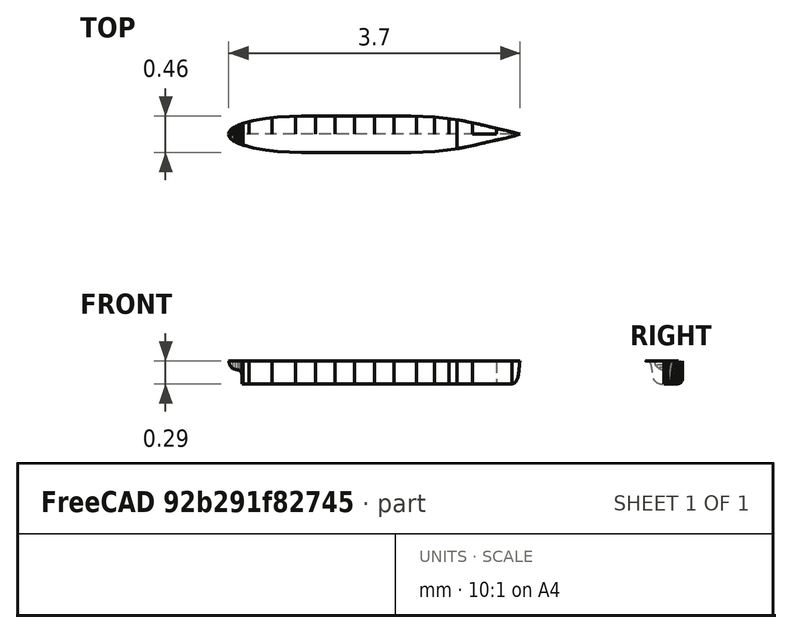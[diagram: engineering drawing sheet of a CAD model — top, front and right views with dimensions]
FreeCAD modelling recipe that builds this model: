
FCSTD DOCUMENT  (FreeCAD 0.21R33771 (Git))
Label: vessel_c
License: All rights reserved
LicenseURL: http://en.wikipedia.org/wiki/All_rights_reserved
objects: Sketcher::SketchObject×36, Part::FeaturePython×20, Surface::Sections×4, Part::Mirroring×2, PartDesign::Body×1, Surface::GeomFillSurface×1, Part::Compound×1
note: 65 computed .brp shape members not serialized (recipe doc carries the construction recipe); baked Part::Feature solids carry a one-line shape summary decoded from their .brp

FEATURE [Sketcher::SketchObject] Sketch
  AttachmentOffset = pos=(0,0,1.849) rot=(0,0,1;0rad)
  FullyConstrained = true
  MapMode = 5
  Placement = pos=(1.849,-4e-16,4e-16) rot=(0.57735,0.57735,0.57735;2.0944rad)
  Support = -> [YZ_Plane]
  sketch-geometry (11):
    g0: LineSegment StartX=0 StartY=0 StartZ=0 EndX=0.1677 EndY=0 EndZ=0
    g1: LineSegment StartX=0 StartY=0.03 StartZ=0 EndX=0.22441 EndY=0.03 EndZ=0
    g2: LineSegment StartX=0 StartY=0.06 StartZ=0 EndX=0.23332 EndY=0.06 EndZ=0
    g3: LineSegment StartX=0 StartY=0.09 StartZ=0 EndX=0.23332 EndY=0.09 EndZ=0
    g4: LineSegment StartX=0 StartY=0.15 StartZ=0 EndX=0.23332 EndY=0.15 EndZ=0
    g5: LineSegment StartX=0 StartY=0.12 StartZ=0 EndX=0.23332 EndY=0.12 EndZ=0
    g6: LineSegment StartX=0 StartY=0.18 StartZ=0 EndX=0.23332 EndY=0.18 EndZ=0
    g7: LineSegment StartX=0 StartY=0.21 StartZ=0 EndX=0.23332 EndY=0.21 EndZ=0
    g8: LineSegment StartX=0 StartY=0.24 StartZ=0 EndX=0.23332 EndY=0.24 EndZ=0
    g9: LineSegment StartX=0 StartY=0.28956 StartZ=0 EndX=0.23332 EndY=0.28956 EndZ=0
    g10: LineSegment StartX=0 StartY=0.27 StartZ=0 EndX=0.23332 EndY=0.27 EndZ=0
  constraints (43):
    c: Coincident(g0,g-1)
    c: PointOnObject(g0,g-1)
    c: PointOnObject(g1,g-2)
    c: Horizontal(g1)
    c: PointOnObject(g2,g-2)
    c: Horizontal(g2)
    c: PointOnObject(g3,g-2)
    c: Horizontal(g3)
    c: PointOnObject(g4,g-2)
    c: Horizontal(g4)
    c: PointOnObject(g5,g-2)
    c: Horizontal(g5)
    c: PointOnObject(g6,g-2)
    c: Horizontal(g6)
    c: PointOnObject(g7,g-2)
    c: Horizontal(g7)
    c: PointOnObject(g8,g-2)
    c: Horizontal(g8)
    c: PointOnObject(g9,g-2)
    c: Horizontal(g9)
    c: DistanceY(g0,g1) = 0.03
    c: DistanceY(g0,g2) = 0.06
    c: DistanceY(g0,g3) = 0.09
    c: DistanceY(g0,g5) = 0.12
    c: DistanceY(g0,g4) = 0.15
    c: DistanceY(g0,g6) = 0.18
    c: DistanceY(g0,g7) = 0.21
    c: DistanceY(g0,g8) = 0.24
    c: DistanceY(g0,g9) = 0.28956
    c: DistanceX(g9,g9) = 0.23332
    c: DistanceX(g8,g8) = 0.23332
    c: DistanceX(g7,g7) = 0.23332
    c: DistanceX(g6,g6) = 0.23332
    c: DistanceX(g4,g4) = 0.23332
    c: DistanceX(g5,g5) = 0.23332
    c: DistanceX(g3,g3) = 0.23332
    c: DistanceX(g2,g2) = 0.23332
    c: DistanceX(g1,g1) = 0.22441
    c: DistanceX(g0,g0) = 0.1677
    c: PointOnObject(g10,g-2)
    c: Horizontal(g10)
    c: DistanceY(g0,g10) = 0.27
    c: DistanceX(g10,g10) = 0.23332
FEATURE [Sketcher::SketchObject] Sketch001
  AttachmentOffset = pos=(0,0,1.59904) rot=(0,0,1;0rad)
  FullyConstrained = true
  MapMode = 5
  Placement = pos=(1.59904,-4e-16,4e-16) rot=(0.57735,0.57735,0.57735;2.0944rad)
  Support = -> [YZ_Plane]
  expr: Constraints[20] = Sketch.Constraints[20]
  expr: Constraints[21] = Sketch.Constraints[21]
  expr: Constraints[22] = Sketch.Constraints[22]
  expr: Constraints[23] = Sketch.Constraints[23]
  expr: Constraints[24] = Sketch.Constraints[24]
  expr: Constraints[25] = Sketch.Constraints[25]
  expr: Constraints[26] = Sketch.Constraints[26]
  expr: Constraints[27] = Sketch.Constraints[27]
  expr: Constraints[28] = Sketch.Constraints[28]
  expr: Constraints[31] = Sketch.Constraints[41]
  sketch-geometry (11):
    g0: LineSegment StartX=0 StartY=0 StartZ=0 EndX=0.15932 EndY=0 EndZ=0
    g1: LineSegment StartX=0 StartY=0.03 StartZ=0 EndX=0.22247 EndY=0.03 EndZ=0
    g2: LineSegment StartX=0 StartY=0.06 StartZ=0 EndX=0.23305 EndY=0.06 EndZ=0
    g3: LineSegment StartX=0 StartY=0.09 StartZ=0 EndX=0.23375 EndY=0.09 EndZ=0
    g4: LineSegment StartX=0 StartY=0.15 StartZ=0 EndX=0.2335 EndY=0.15 EndZ=0
    g5: LineSegment StartX=0 StartY=0.12 StartZ=0 EndX=0.23366 EndY=0.12 EndZ=0
    g6: LineSegment StartX=0 StartY=0.18 StartZ=0 EndX=0.23339 EndY=0.18 EndZ=0
    g7: LineSegment StartX=0 StartY=0.21 StartZ=0 EndX=0.23332 EndY=0.21 EndZ=0
    g8: LineSegment StartX=0 StartY=0.24 StartZ=0 EndX=0.23329 EndY=0.24 EndZ=0
    g9: LineSegment StartX=0 StartY=0.28956 StartZ=0 EndX=0.23334 EndY=0.28956 EndZ=0
    g10: LineSegment StartX=0 StartY=0.27 StartZ=0 EndX=0.23332 EndY=0.27 EndZ=0
  constraints (43):
    c: Coincident(g0,g-1)
    c: PointOnObject(g0,g-1)
    c: PointOnObject(g1,g-2)
    c: Horizontal(g1)
    c: PointOnObject(g2,g-2)
    c: Horizontal(g2)
    c: PointOnObject(g3,g-2)
    c: Horizontal(g3)
    c: PointOnObject(g4,g-2)
    c: Horizontal(g4)
    c: PointOnObject(g5,g-2)
    c: Horizontal(g5)
    c: PointOnObject(g6,g-2)
    c: Horizontal(g6)
    c: PointOnObject(g7,g-2)
    c: Horizontal(g7)
    c: PointOnObject(g8,g-2)
    c: Horizontal(g8)
    c: PointOnObject(g9,g-2)
    c: Horizontal(g9)
    c: DistanceY(g0,g1) = 0.03
    c: DistanceY(g0,g2) = 0.06
    c: DistanceY(g0,g3) = 0.09
    c: DistanceY(g0,g5) = 0.12
    c: DistanceY(g0,g4) = 0.15
    c: DistanceY(g0,g6) = 0.18
    c: DistanceY(g0,g7) = 0.21
    c: DistanceY(g0,g8) = 0.24
    c: DistanceY(g0,g9) = 0.28956
    c: PointOnObject(g10,g-2)
    c: Horizontal(g10)
    c: DistanceY(g0,g10) = 0.27
    c: DistanceX(g9,g9) = 0.23334
    c: DistanceX(g10,g10) = 0.23332
    c: DistanceX(g8,g8) = 0.23329
    c: DistanceX(g7,g7) = 0.23332
    c: DistanceX(g6,g6) = 0.23339
    c: DistanceX(g4,g4) = 0.2335
    c: DistanceX(g5,g5) = 0.23366
    c: DistanceX(g3,g3) = 0.23375
    c: DistanceX(g2,g2) = 0.23305
    c: DistanceX(g1,g1) = 0.22247
    c: DistanceX(g0,g0) = 0.15932
FEATURE [Sketcher::SketchObject] Sketch002
  AttachmentOffset = pos=(0,0,1.34904) rot=(0,0,1;0rad)
  FullyConstrained = true
  MapMode = 5
  Placement = pos=(1.34904,-3e-16,3e-16) rot=(0.57735,0.57735,0.57735;2.0944rad)
  Support = -> [YZ_Plane]
  expr: Constraints[20] = Sketch.Constraints[20]
  expr: Constraints[21] = Sketch.Constraints[21]
  expr: Constraints[22] = Sketch.Constraints[22]
  expr: Constraints[23] = Sketch.Constraints[23]
  expr: Constraints[24] = Sketch.Constraints[24]
  expr: Constraints[25] = Sketch.Constraints[25]
  expr: Constraints[26] = Sketch.Constraints[26]
  expr: Constraints[27] = Sketch.Constraints[27]
  expr: Constraints[28] = Sketch.Constraints[28]
  expr: Constraints[31] = Sketch.Constraints[41]
  sketch-geometry (11):
    g0: LineSegment StartX=0 StartY=0 StartZ=0 EndX=0.14688 EndY=0 EndZ=0
    g1: LineSegment StartX=0 StartY=0.03 StartZ=0 EndX=0.20812 EndY=0.03 EndZ=0
    g2: LineSegment StartX=0 StartY=0.06 StartZ=0 EndX=0.2252 EndY=0.06 EndZ=0
    g3: LineSegment StartX=0 StartY=0.09 StartZ=0 EndX=0.23076 EndY=0.09 EndZ=0
    g4: LineSegment StartX=0 StartY=0.15 StartZ=0 EndX=0.23278 EndY=0.15 EndZ=0
    g5: LineSegment StartX=0 StartY=0.12 StartZ=0 EndX=0.23256 EndY=0.12 EndZ=0
    g6: LineSegment StartX=0 StartY=0.18 StartZ=0 EndX=0.23278 EndY=0.18 EndZ=0
    g7: LineSegment StartX=0 StartY=0.21 StartZ=0 EndX=0.23286 EndY=0.21 EndZ=0
    g8: LineSegment StartX=0 StartY=0.24 StartZ=0 EndX=0.23303 EndY=0.24 EndZ=0
    g9: LineSegment StartX=0 StartY=0.28956 StartZ=0 EndX=0.23331 EndY=0.28956 EndZ=0
    g10: LineSegment StartX=0 StartY=0.27 StartZ=0 EndX=0.2332 EndY=0.27 EndZ=0
  constraints (43):
    c: Coincident(g0,g-1)
    c: PointOnObject(g0,g-1)
    c: PointOnObject(g1,g-2)
    c: Horizontal(g1)
    c: PointOnObject(g2,g-2)
    c: Horizontal(g2)
    c: PointOnObject(g3,g-2)
    c: Horizontal(g3)
    c: PointOnObject(g4,g-2)
    c: Horizontal(g4)
    c: PointOnObject(g5,g-2)
    c: Horizontal(g5)
    c: PointOnObject(g6,g-2)
    c: Horizontal(g6)
    c: PointOnObject(g7,g-2)
    c: Horizontal(g7)
    c: PointOnObject(g8,g-2)
    c: Horizontal(g8)
    c: PointOnObject(g9,g-2)
    c: Horizontal(g9)
    c: DistanceY(g0,g1) = 0.03
    c: DistanceY(g0,g2) = 0.06
    c: DistanceY(g0,g3) = 0.09
    c: DistanceY(g0,g5) = 0.12
    c: DistanceY(g0,g4) = 0.15
    c: DistanceY(g0,g6) = 0.18
    c: DistanceY(g0,g7) = 0.21
    c: DistanceY(g0,g8) = 0.24
    c: DistanceY(g0,g9) = 0.28956
    c: PointOnObject(g10,g-2)
    c: Horizontal(g10)
    c: DistanceY(g0,g10) = 0.27
    c: DistanceX(g9,g9) = 0.23331
    c: DistanceX(g10,g10) = 0.2332
    c: DistanceX(g8,g8) = 0.23303
    c: DistanceX(g7,g7) = 0.23286
    c: DistanceX(g6,g6) = 0.23278
    c: DistanceX(g4,g4) = 0.23278
    c: DistanceX(g5,g5) = 0.23256
    c: DistanceX(g3,g3) = 0.23076
    c: DistanceX(g2,g2) = 0.2252
    c: DistanceX(g1,g1) = 0.20812
    c: DistanceX(g0,g0) = 0.14688
FEATURE [Sketcher::SketchObject] Sketch003
  AttachmentOffset = pos=(0,0,1.09904) rot=(0,0,1;0rad)
  FullyConstrained = false
  MapMode = 5
  Placement = pos=(1.09904,-2e-16,2e-16) rot=(0.57735,0.57735,0.57735;2.0944rad)
  Support = -> [YZ_Plane]
  expr: Constraints[19] = Sketch.Constraints[20]
  expr: Constraints[20] = Sketch.Constraints[21]
  expr: Constraints[21] = Sketch.Constraints[22]
  expr: Constraints[22] = Sketch.Constraints[23]
  expr: Constraints[23] = Sketch.Constraints[24]
  expr: Constraints[24] = Sketch.Constraints[25]
  expr: Constraints[25] = Sketch.Constraints[26]
  expr: Constraints[26] = Sketch.Constraints[27]
  expr: Constraints[27] = Sketch.Constraints[28]
  expr: Constraints[30] = Sketch.Constraints[41]
  sketch-geometry (11):
    g0: LineSegment StartX=0 StartY=0 StartZ=0 EndX=0.09104 EndY=0 EndZ=0
    g1: LineSegment StartX=0 StartY=0.03 StartZ=0 EndX=0.17694 EndY=0.03 EndZ=0
    g2: LineSegment StartX=0 StartY=0.06 StartZ=0 EndX=0.19948 EndY=0.06 EndZ=0
    g3: LineSegment StartX=0 StartY=0.09 StartZ=0 EndX=0.21112 EndY=0.09 EndZ=0
    g4: LineSegment StartX=0 StartY=0.15 StartZ=0 EndX=0.22462 EndY=0.15 EndZ=0
    g5: LineSegment StartX=0 StartY=0.12 StartZ=0 EndX=0.21892 EndY=0.12 EndZ=0
    g6: LineSegment StartX=0 StartY=0.18 StartZ=0 EndX=0.2284 EndY=0.18 EndZ=0
    g7: LineSegment StartX=0 StartY=0.21 StartZ=0 EndX=0.23059 EndY=0.21 EndZ=0
    g8: LineSegment StartX=0 StartY=0.24 StartZ=0 EndX=0.23175 EndY=0.24 EndZ=0
    g9: LineSegment StartX=0 StartY=0.28956 StartZ=0 EndX=0.23316 EndY=0.28956 EndZ=0
    g10: LineSegment StartX=0 StartY=0.27 StartZ=0 EndX=0.23261 EndY=0.27 EndZ=0
  constraints (42):
    c: Coincident(g0,g-1)
    c: PointOnObject(g0,g-1)
    c: PointOnObject(g1,g-2)
    c: Horizontal(g1)
    c: PointOnObject(g2,g-2)
    c: Horizontal(g2)
    c: PointOnObject(g3,g-2)
    c: Horizontal(g3)
    c: PointOnObject(g4,g-2)
    c: Horizontal(g4)
    c: PointOnObject(g5,g-2)
    c: Horizontal(g5)
    c: PointOnObject(g6,g-2)
    c: Horizontal(g6)
    c: PointOnObject(g7,g-2)
    c: Horizontal(g7)
    c: PointOnObject(g8,g-2)
    c: Horizontal(g8)
    c: PointOnObject(g9,g-2)
    c: DistanceY(g0,g1) = 0.03
    c: DistanceY(g0,g2) = 0.06
    c: DistanceY(g0,g3) = 0.09
    c: DistanceY(g0,g5) = 0.12
    c: DistanceY(g0,g4) = 0.15
    c: DistanceY(g0,g6) = 0.18
    c: DistanceY(g0,g7) = 0.21
    c: DistanceY(g0,g8) = 0.24
    c: DistanceY(g0,g9) = 0.28956
    c: PointOnObject(g10,g-2)
    c: Horizontal(g10)
    c: DistanceY(g0,g10) = 0.27
    c: DistanceX(g9,g9) = 0.23316
    c: DistanceX(g10,g10) = 0.23261
    c: DistanceX(g8,g8) = 0.23175
    c: DistanceX(g7,g7) = 0.23059
    c: DistanceX(g6,g6) = 0.2284
    c: DistanceX(g4,g4) = 0.22462
    c: DistanceX(g5,g5) = 0.21892
    c: DistanceX(g3,g3) = 0.21112
    c: DistanceX(g2,g2) = 0.19948
    c: DistanceX(g1,g1) = 0.17694
    c: DistanceX(g0,g0) = 0.09104
FEATURE [Sketcher::SketchObject] Sketch004
  AttachmentOffset = pos=(0,0,0.84904) rot=(0,0,1;0rad)
  FullyConstrained = true
  MapMode = 5
  Placement = pos=(0.84904,-2e-16,2e-16) rot=(0.57735,0.57735,0.57735;2.0944rad)
  Support = -> [YZ_Plane]
  expr: Constraints[20] = Sketch.Constraints[20]
  expr: Constraints[21] = Sketch.Constraints[21]
  expr: Constraints[22] = Sketch.Constraints[22]
  expr: Constraints[23] = Sketch.Constraints[23]
  expr: Constraints[24] = Sketch.Constraints[24]
  expr: Constraints[25] = Sketch.Constraints[25]
  expr: Constraints[26] = Sketch.Constraints[26]
  expr: Constraints[27] = Sketch.Constraints[27]
  expr: Constraints[28] = Sketch.Constraints[28]
  expr: Constraints[31] = Sketch.Constraints[41]
  sketch-geometry (11):
    g0: LineSegment StartX=0 StartY=0 StartZ=0 EndX=0.06115 EndY=0 EndZ=0
    g1: LineSegment StartX=0 StartY=0.03 StartZ=0 EndX=0.12995 EndY=0.03 EndZ=0
    g2: LineSegment StartX=0 StartY=0.06 StartZ=0 EndX=0.1539 EndY=0.06 EndZ=0
    g3: LineSegment StartX=0 StartY=0.09 StartZ=0 EndX=0.17069 EndY=0.09 EndZ=0
    g4: LineSegment StartX=0 StartY=0.15 StartZ=0 EndX=0.19808 EndY=0.15 EndZ=0
    g5: LineSegment StartX=0 StartY=0.12 StartZ=0 EndX=0.18532 EndY=0.12 EndZ=0
    g6: LineSegment StartX=0 StartY=0.18 StartZ=0 EndX=0.20831 EndY=0.18 EndZ=0
    g7: LineSegment StartX=0 StartY=0.21 StartZ=0 EndX=0.21679 EndY=0.21 EndZ=0
    g8: LineSegment StartX=0 StartY=0.24 StartZ=0 EndX=0.2234 EndY=0.24 EndZ=0
    g9: LineSegment StartX=0 StartY=0.28956 StartZ=0 EndX=0.23047 EndY=0.28956 EndZ=0
    g10: LineSegment StartX=0 StartY=0.27 StartZ=0 EndX=0.22818 EndY=0.27 EndZ=0
  constraints (43):
    c: Coincident(g0,g-1)
    c: PointOnObject(g0,g-1)
    c: PointOnObject(g1,g-2)
    c: Horizontal(g1)
    c: PointOnObject(g2,g-2)
    c: Horizontal(g2)
    c: PointOnObject(g3,g-2)
    c: Horizontal(g3)
    c: PointOnObject(g4,g-2)
    c: Horizontal(g4)
    c: PointOnObject(g5,g-2)
    c: Horizontal(g5)
    c: PointOnObject(g6,g-2)
    c: Horizontal(g6)
    c: PointOnObject(g7,g-2)
    c: Horizontal(g7)
    c: PointOnObject(g8,g-2)
    c: Horizontal(g8)
    c: PointOnObject(g9,g-2)
    c: Horizontal(g9)
    c: DistanceY(g0,g1) = 0.03
    c: DistanceY(g0,g2) = 0.06
    c: DistanceY(g0,g3) = 0.09
    c: DistanceY(g0,g5) = 0.12
    c: DistanceY(g0,g4) = 0.15
    c: DistanceY(g0,g6) = 0.18
    c: DistanceY(g0,g7) = 0.21
    c: DistanceY(g0,g8) = 0.24
    c: DistanceY(g0,g9) = 0.28956
    c: PointOnObject(g10,g-2)
    c: Horizontal(g10)
    c: DistanceY(g0,g10) = 0.27
    c: DistanceX(g9,g9) = 0.23047
    c: DistanceX(g10,g10) = 0.22818
    c: DistanceX(g8,g8) = 0.2234
    c: DistanceX(g7,g7) = 0.21679
    c: DistanceX(g6,g6) = 0.20831
    c: DistanceX(g4,g4) = 0.19808
    c: DistanceX(g5,g5) = 0.18532
    c: DistanceX(g3,g3) = 0.17069
    c: DistanceX(g2,g2) = 0.1539
    c: DistanceX(g1,g1) = 0.12995
    c: DistanceX(g0,g0) = 0.06115
FEATURE [Sketcher::SketchObject] Sketch005
  AttachmentOffset = pos=(0,0,0.54904) rot=(0,0,1;0rad)
  FullyConstrained = true
  MapMode = 5
  Placement = pos=(0.54904,-1e-16,1e-16) rot=(0.57735,0.57735,0.57735;2.0944rad)
  Support = -> [YZ_Plane]
  expr: Constraints[20] = Sketch.Constraints[20]
  expr: Constraints[21] = Sketch.Constraints[21]
  expr: Constraints[22] = Sketch.Constraints[22]
  expr: Constraints[23] = Sketch.Constraints[23]
  expr: Constraints[24] = Sketch.Constraints[24]
  expr: Constraints[25] = Sketch.Constraints[25]
  expr: Constraints[26] = Sketch.Constraints[26]
  expr: Constraints[27] = Sketch.Constraints[27]
  expr: Constraints[28] = Sketch.Constraints[28]
  expr: Constraints[31] = Sketch.Constraints[41]
  sketch-geometry (11):
    g0: LineSegment StartX=0 StartY=0 StartZ=0 EndX=0.02137 EndY=0 EndZ=0
    g1: LineSegment StartX=0 StartY=0.03 StartZ=0 EndX=0.06895 EndY=0.03 EndZ=0
    g2: LineSegment StartX=0 StartY=0.06 StartZ=0 EndX=0.08376 EndY=0.06 EndZ=0
    g3: LineSegment StartX=0 StartY=0.09 StartZ=0 EndX=0.09573 EndY=0.09 EndZ=0
    g4: LineSegment StartX=0 StartY=0.15 StartZ=0 EndX=0.13284 EndY=0.15 EndZ=0
    g5: LineSegment StartX=0 StartY=0.12 StartZ=0 EndX=0.11144 EndY=0.12 EndZ=0
    g6: LineSegment StartX=0 StartY=0.18 StartZ=0 EndX=0.15604 EndY=0.18 EndZ=0
    g7: LineSegment StartX=0 StartY=0.21 StartZ=0 EndX=0.17731 EndY=0.21 EndZ=0
    g8: LineSegment StartX=0 StartY=0.24 StartZ=0 EndX=0.19393 EndY=0.24 EndZ=0
    g9: LineSegment StartX=0 StartY=0.28956 StartZ=0 EndX=0.21151 EndY=0.28956 EndZ=0
    g10: LineSegment StartX=0 StartY=0.27 StartZ=0 EndX=0.20301 EndY=0.27 EndZ=0
  constraints (43):
    c: Coincident(g0,g-1)
    c: PointOnObject(g0,g-1)
    c: PointOnObject(g1,g-2)
    c: Horizontal(g1)
    c: PointOnObject(g2,g-2)
    c: Horizontal(g2)
    c: PointOnObject(g3,g-2)
    c: Horizontal(g3)
    c: PointOnObject(g4,g-2)
    c: Horizontal(g4)
    c: PointOnObject(g5,g-2)
    c: Horizontal(g5)
    c: PointOnObject(g6,g-2)
    c: Horizontal(g6)
    c: PointOnObject(g7,g-2)
    c: Horizontal(g7)
    c: PointOnObject(g8,g-2)
    c: Horizontal(g8)
    c: PointOnObject(g9,g-2)
    c: Horizontal(g9)
    c: DistanceY(g0,g1) = 0.03
    c: DistanceY(g0,g2) = 0.06
    c: DistanceY(g0,g3) = 0.09
    c: DistanceY(g0,g5) = 0.12
    c: DistanceY(g0,g4) = 0.15
    c: DistanceY(g0,g6) = 0.18
    c: DistanceY(g0,g7) = 0.21
    c: DistanceY(g0,g8) = 0.24
    c: DistanceY(g0,g9) = 0.28956
    c: PointOnObject(g10,g-2)
    c: Horizontal(g10)
    c: DistanceY(g0,g10) = 0.27
    c: DistanceX(g9,g9) = 0.21151
    c: DistanceX(g10,g10) = 0.20301
    c: DistanceX(g8,g8) = 0.19393
    c: DistanceX(g7,g7) = 0.17731
    c: DistanceX(g6,g6) = 0.15604
    c: DistanceX(g4,g4) = 0.13284
    c: DistanceX(g5,g5) = 0.11144
    c: DistanceX(g3,g3) = 0.09573
    c: DistanceX(g2,g2) = 0.08376
    c: DistanceX(g1,g1) = 0.06895
    c: DistanceX(g0,g0) = 0.02137
FEATURE [Sketcher::SketchObject] Sketch006
  AttachmentOffset = pos=(0,0,0.25904) rot=(0,0,1;0rad)
  FullyConstrained = true
  MapMode = 5
  Placement = pos=(0.25904,-1e-16,1e-16) rot=(0.57735,0.57735,0.57735;2.0944rad)
  Support = -> [YZ_Plane]
  expr: Constraints[20] = Sketch.Constraints[20]
  expr: Constraints[21] = Sketch.Constraints[21]
  expr: Constraints[22] = Sketch.Constraints[22]
  expr: Constraints[23] = Sketch.Constraints[23]
  expr: Constraints[24] = Sketch.Constraints[24]
  expr: Constraints[25] = Sketch.Constraints[25]
  expr: Constraints[26] = Sketch.Constraints[26]
  expr: Constraints[27] = Sketch.Constraints[27]
  expr: Constraints[28] = Sketch.Constraints[28]
  expr: Constraints[31] = Sketch.Constraints[41]
  sketch-geometry (11):
    g0: LineSegment StartX=0 StartY=0 StartZ=0 EndX=2e-16 EndY=0 EndZ=0
    g1: LineSegment StartX=0 StartY=0.03 StartZ=0 EndX=0.0157 EndY=0.03 EndZ=0
    g2: LineSegment StartX=0 StartY=0.06 StartZ=0 EndX=0.01924 EndY=0.06 EndZ=0
    g3: LineSegment StartX=0 StartY=0.09 StartZ=0 EndX=0.02165 EndY=0.09 EndZ=0
    g4: LineSegment StartX=0 StartY=0.15 StartZ=0 EndX=0.03857 EndY=0.15 EndZ=0
    g5: LineSegment StartX=0 StartY=0.12 StartZ=0 EndX=0.02638 EndY=0.12 EndZ=0
    g6: LineSegment StartX=0 StartY=0.18 StartZ=0 EndX=0.071 EndY=0.18 EndZ=0
    g7: LineSegment StartX=0 StartY=0.21 StartZ=0 EndX=0.10659 EndY=0.21 EndZ=0
    g8: LineSegment StartX=0 StartY=0.24 StartZ=0 EndX=0.13225 EndY=0.24 EndZ=0
    g9: LineSegment StartX=0 StartY=0.28956 StartZ=0 EndX=0.16167 EndY=0.28956 EndZ=0
    g10: LineSegment StartX=0 StartY=0.27 StartZ=0 EndX=0.15151 EndY=0.27 EndZ=0
  constraints (43):
    c: Coincident(g0,g-1)
    c: PointOnObject(g0,g-1)
    c: PointOnObject(g1,g-2)
    c: Horizontal(g1)
    c: PointOnObject(g2,g-2)
    c: Horizontal(g2)
    c: PointOnObject(g3,g-2)
    c: Horizontal(g3)
    c: PointOnObject(g4,g-2)
    c: Horizontal(g4)
    c: PointOnObject(g5,g-2)
    c: Horizontal(g5)
    c: PointOnObject(g6,g-2)
    c: Horizontal(g6)
    c: PointOnObject(g7,g-2)
    c: Horizontal(g7)
    c: PointOnObject(g8,g-2)
    c: Horizontal(g8)
    c: PointOnObject(g9,g-2)
    c: Horizontal(g9)
    c: DistanceY(g0,g1) = 0.03
    c: DistanceY(g0,g2) = 0.06
    c: DistanceY(g0,g3) = 0.09
    c: DistanceY(g0,g5) = 0.12
    c: DistanceY(g0,g4) = 0.15
    c: DistanceY(g0,g6) = 0.18
    c: DistanceY(g0,g7) = 0.21
    c: DistanceY(g0,g8) = 0.24
    c: DistanceY(g0,g9) = 0.28956
    c: PointOnObject(g10,g-2)
    c: Horizontal(g10)
    c: DistanceY(g0,g10) = 0.27
    c: DistanceX(g9,g9) = 0.16167
    c: DistanceX(g10,g10) = 0.15151
    c: DistanceX(g8,g8) = 0.13225
    c: DistanceX(g7,g7) = 0.10659
    c: DistanceX(g6,g6) = 0.071
    c: DistanceX(g4,g4) = 0.03857
    c: DistanceX(g5,g5) = 0.02638
    c: DistanceX(g3,g3) = 0.02165
    c: DistanceX(g2,g2) = 0.01924
    c: DistanceX(g1,g1) = 0.0157
    c: DistanceX(g0,g0) = 0
FEATURE [Sketcher::SketchObject] Sketch008
  AttachmentOffset = pos=(0,0,0.16724) rot=(0,0,1;0rad)
  FullyConstrained = false
  MapMode = 5
  Placement = pos=(0.16724,0,0) rot=(0.57735,0.57735,0.57735;2.0944rad)
  Support = -> [YZ_Plane]
  expr: Constraints[10] = Sketch.Constraints[24]
  expr: Constraints[11] = Sketch.Constraints[25]
  expr: Constraints[12] = Sketch.Constraints[26]
  expr: Constraints[13] = Sketch.Constraints[27]
  expr: Constraints[14] = Sketch.Constraints[28]
  expr: Constraints[17] = Sketch.Constraints[41]
  sketch-geometry (43):
    g0: LineSegment StartX=0 StartY=0.15 StartZ=0 EndX=0.003 EndY=0.15 EndZ=0
    g1: LineSegment StartX=0 StartY=0.18 StartZ=0 EndX=0.03677 EndY=0.18 EndZ=0
    g2: LineSegment StartX=0 StartY=0.21 StartZ=0 EndX=0.08149 EndY=0.21 EndZ=0
    g3: LineSegment StartX=0 StartY=0.24 StartZ=0 EndX=0.10547 EndY=0.24 EndZ=0
    g4: LineSegment StartX=0 StartY=0.28956 StartZ=0 EndX=0.13305 EndY=0.28956 EndZ=0
    g5: LineSegment StartX=0 StartY=0.27 StartZ=0 EndX=0.12303 EndY=0.27 EndZ=0
    g6: GeomPoint X=0 Y=0.12633 Z=0
    g7: LineSegment StartX=0 StartY=0.150003 StartZ=0 EndX=-0.00387781 EndY=0.150003 EndZ=0
    g8: LineSegment StartX=0 StartY=0.18 StartZ=0 EndX=-0.0366718 EndY=0.18 EndZ=0
    g9: LineSegment StartX=0 StartY=0.21 StartZ=0 EndX=-0.0814964 EndY=0.21 EndZ=0
    g10: LineSegment StartX=0 StartY=0.24 StartZ=0 EndX=-0.10547 EndY=0.24 EndZ=0
    g11: LineSegment StartX=0 StartY=0.28956 StartZ=0 EndX=-0.13305 EndY=0.28956 EndZ=0
    g12: LineSegment StartX=0 StartY=0.27 StartZ=0 EndX=-0.12303 EndY=0.27 EndZ=0
    g13: GeomPoint X=0 Y=0.12633 Z=0
    g14-g26: GeomPoint x13 (B-spline internal-alignment scaffolding for g27; pole/knot coordinates omitted)
    g27: BSplineCurve PolesCount=15 KnotsCount=13 Degree=3 IsPeriodic=0
    g28-g42: Circle x15 (B-spline internal-alignment scaffolding for g27; pole/knot coordinates omitted)
  constraints (75):
    c: PointOnObject(g0,g-2)
    c: Horizontal(g0)
    c: PointOnObject(g1,g-2)
    c: Horizontal(g1)
    c: PointOnObject(g2,g-2)
    c: Horizontal(g2)
    c: PointOnObject(g3,g-2)
    c: Horizontal(g3)
    c: PointOnObject(g4,g-2)
    c: Horizontal(g4)
    c: DistanceY(g-1,g0) = 0.15
    c: DistanceY(g-1,g1) = 0.18
    c: DistanceY(g-1,g2) = 0.21
    c: DistanceY(g-1,g3) = 0.24
    c: DistanceY(g-1,g4) = 0.28956
    c: PointOnObject(g5,g-2)
    c: Horizontal(g5)
    c: DistanceY(g-1,g5) = 0.27
    c: DistanceX(g4,g4) = 0.13305
    c: DistanceX(g5,g5) = 0.12303
    c: DistanceX(g3,g3) = 0.10547
    c: DistanceX(g2,g2) = 0.08149
    c: DistanceX(g1,g1) = 0.03677
    c: DistanceX(g0,g0) = 0.003
    c: PointOnObject(g6,g-2)
    c: Horizontal(g7)
    c: Horizontal(g8)
    c: Horizontal(g9)
    c: Horizontal(g10)
    c: Horizontal(g11)
    c: Horizontal(g12)
    c: Coincident(g27,g4)
    c: Coincident(g15,g5)
    c: Coincident(g16,g3)
    c: Coincident(g17,g2)
    c: Coincident(g18,g1)
    c: Coincident(g19,g0)
    c: Coincident(g20,g6)
    c: Coincident(g21,g7)
    c: Coincident(g22,g8)
    c: Coincident(g23,g9)
    c: Coincident(g24,g10)
    c: Coincident(g25,g12)
    c: Coincident(g27,g11)
    c: InternalAlignment(g14-g26 -> g27) x13
    c: InternalAlignment(g28,g27)
    c: Weight(g28) = 1
    c: InternalAlignment(g29,g27)
    c: Equal(g29,g28)
    c: InternalAlignment(g30,g27)
    c: Equal(g30,g28)
    c: InternalAlignment(g31,g27)
    c: Equal(g31,g28)
    c: InternalAlignment(g32,g27)
    c: Equal(g32,g28)
    c: InternalAlignment(g33,g27)
    c: Equal(g33,g28)
    c: InternalAlignment(g34,g27)
    c: Equal(g34,g28)
    c: InternalAlignment(g35,g27)
    c: Equal(g35,g28)
    c: InternalAlignment(g36,g27)
    c: Equal(g36,g28)
    c: InternalAlignment(g37,g27)
    c: Equal(g37,g28)
    c: InternalAlignment(g38,g27)
    c: Equal(g38,g28)
    c: InternalAlignment(g39,g27)
    c: Equal(g39,g28)
    c: InternalAlignment(g40,g27)
    c: Equal(g40,g28)
    c: InternalAlignment(g41,g27)
    c: Equal(g41,g28)
    c: InternalAlignment(g42,g27)
    c: Equal(g42,g28)
FEATURE [Sketcher::SketchObject] Sketch012
  AttachmentOffset = pos=(0,0,0.079) rot=(0,0,1;0rad)
  FullyConstrained = false
  MapMode = 5
  Placement = pos=(0.079,0,0) rot=(0.57735,0.57735,0.57735;2.0944rad)
  Support = -> [YZ_Plane]
  sketch-geometry (31):
    g0: LineSegment StartX=0 StartY=0.21 StartZ=0 EndX=0.04561 EndY=0.21 EndZ=0
    g1: LineSegment StartX=0 StartY=0.24 StartZ=0 EndX=0.0687 EndY=0.24 EndZ=0
    g2: LineSegment StartX=0 StartY=0.28956 StartZ=0 EndX=0.09553 EndY=0.28956 EndZ=0
    g3: LineSegment StartX=0 StartY=0.27 StartZ=0 EndX=0.08547 EndY=0.27 EndZ=0
    g4: GeomPoint X=0 Y=0.18381 Z=0
    g5: LineSegment StartX=0 StartY=0.21 StartZ=0 EndX=-0.04561 EndY=0.21 EndZ=0
    g6: LineSegment StartX=0 StartY=0.24 StartZ=0 EndX=-0.0687 EndY=0.24 EndZ=0
    g7: LineSegment StartX=0 StartY=0.28956 StartZ=0 EndX=-0.09553 EndY=0.28956 EndZ=0
    g8: LineSegment StartX=0 StartY=0.27 StartZ=0 EndX=-0.08547 EndY=0.27 EndZ=0
    g9: GeomPoint X=0 Y=0.18381 Z=0
    g10-g18: GeomPoint x9 (B-spline internal-alignment scaffolding for g19; pole/knot coordinates omitted)
    g19: BSplineCurve PolesCount=11 KnotsCount=9 Degree=3 IsPeriodic=0
    g20-g30: Circle x11 (B-spline internal-alignment scaffolding for g19; pole/knot coordinates omitted)
  constraints (49):
    c: PointOnObject(g0,g-2)
    c: Horizontal(g0)
    c: PointOnObject(g1,g-2)
    c: Horizontal(g1)
    c: PointOnObject(g2,g-2)
    c: Horizontal(g2)
    c: PointOnObject(g3,g-2)
    c: Horizontal(g3)
    c: DistanceX(g2,g2) = 0.09553
    c: DistanceX(g3,g3) = 0.08547
    c: DistanceX(g1,g1) = 0.0687
    c: DistanceX(g0,g0) = 0.04561
    c: PointOnObject(g4,g-2)
    c: Horizontal(g5)
    c: Horizontal(g6)
    c: Horizontal(g7)
    c: Horizontal(g8)
    c: Coincident(g19,g2)
    c: Coincident(g11,g3)
    c: Coincident(g12,g1)
    c: Coincident(g13,g0)
    c: Coincident(g14,g4)
    c: Coincident(g15,g5)
    c: Coincident(g16,g6)
    c: Coincident(g17,g8)
    c: Coincident(g19,g7)
    c: InternalAlignment(g10-g18 -> g19) x9
    c: InternalAlignment(g20,g19)
    c: Weight(g20) = 1
    c: InternalAlignment(g21,g19)
    c: Equal(g21,g20)
    c: InternalAlignment(g22,g19)
    c: Equal(g22,g20)
    c: InternalAlignment(g23,g19)
    c: Equal(g23,g20)
    c: InternalAlignment(g24,g19)
    c: Equal(g24,g20)
    c: InternalAlignment(g25,g19)
    c: Equal(g25,g20)
    c: InternalAlignment(g26,g19)
    c: Equal(g26,g20)
    c: InternalAlignment(g27,g19)
    c: Equal(g27,g20)
    c: InternalAlignment(g28,g19)
    c: Equal(g28,g20)
    c: InternalAlignment(g29,g19)
    c: Equal(g29,g20)
    c: InternalAlignment(g30,g19)
    c: Equal(g30,g20)
FEATURE [Sketcher::SketchObject] Sketch013
  AttachmentOffset = pos=(0,0,0.01904) rot=(0,0,1;0rad)
  FullyConstrained = false
  MapMode = 5
  Placement = pos=(0.01904,0,0) rot=(0.57735,0.57735,0.57735;2.0944rad)
  Support = -> [YZ_Plane]
  sketch-geometry (8):
    g0: LineSegment StartX=0 StartY=0.24 StartZ=0 EndX=0.013 EndY=0.24 EndZ=0
    g1: LineSegment StartX=0 StartY=0.28956 StartZ=0 EndX=0.04927 EndY=0.28956 EndZ=0
    g2: LineSegment StartX=0 StartY=0.27 StartZ=0 EndX=0.0368 EndY=0.27 EndZ=0
    g3: GeomPoint X=0 Y=0.22911 Z=0
    g4: LineSegment StartX=0 StartY=0.24 StartZ=0 EndX=-0.013 EndY=0.24 EndZ=0
    g5: LineSegment StartX=0 StartY=0.28956 StartZ=0 EndX=-0.04927 EndY=0.28956 EndZ=0
    g6: GeomPoint X=0 Y=0.22911 Z=0
    g7: LineSegment StartX=-0.04927 StartY=0.28956 StartZ=0 EndX=0.04927 EndY=0.28956 EndZ=0
  constraints (16):
    c: PointOnObject(g0,g-2)
    c: Horizontal(g0)
    c: PointOnObject(g1,g-2)
    c: Horizontal(g1)
    c: PointOnObject(g2,g-2)
    c: Horizontal(g2)
    c: DistanceX(g1,g1) = 0.04927
    c: DistanceX(g2,g2) = 0.0368
    c: DistanceX(g0,g0) = 0.013
    c: PointOnObject(g3,g-2)
    c: DistanceY(g-1,g3) = 0.22911
    c: Horizontal(g4)
    c: Horizontal(g5)
    c: Coincident(g7,g5)
    c: Coincident(g7,g1)
    c: Horizontal(g7)
FEATURE [Sketcher::SketchObject] Sketch016
  AttachmentOffset = pos=(0,0,2.09904) rot=(0,0,1;0rad)
  FullyConstrained = true
  MapMode = 5
  Placement = pos=(2.09904,-5e-16,5e-16) rot=(0.57735,0.57735,0.57735;2.0944rad)
  Support = -> [YZ_Plane]
  expr: Constraints[20] = Sketch.Constraints[20]
  expr: Constraints[21] = Sketch.Constraints[21]
  expr: Constraints[22] = Sketch.Constraints[22]
  expr: Constraints[23] = Sketch.Constraints[23]
  expr: Constraints[24] = Sketch.Constraints[24]
  expr: Constraints[25] = Sketch.Constraints[25]
  expr: Constraints[26] = Sketch.Constraints[26]
  expr: Constraints[27] = Sketch.Constraints[27]
  expr: Constraints[28] = Sketch.Constraints[28]
  expr: Constraints[31] = Sketch.Constraints[41]
  sketch-geometry (11):
    g0: LineSegment StartX=0 StartY=0 StartZ=0 EndX=0.15932 EndY=0 EndZ=0
    g1: LineSegment StartX=0 StartY=0.03 StartZ=0 EndX=0.22247 EndY=0.03 EndZ=0
    g2: LineSegment StartX=0 StartY=0.06 StartZ=0 EndX=0.23305 EndY=0.06 EndZ=0
    g3: LineSegment StartX=0 StartY=0.09 StartZ=0 EndX=0.23375 EndY=0.09 EndZ=0
    g4: LineSegment StartX=0 StartY=0.15 StartZ=0 EndX=0.2335 EndY=0.15 EndZ=0
    g5: LineSegment StartX=0 StartY=0.12 StartZ=0 EndX=0.23366 EndY=0.12 EndZ=0
    g6: LineSegment StartX=0 StartY=0.18 StartZ=0 EndX=0.23339 EndY=0.18 EndZ=0
    g7: LineSegment StartX=0 StartY=0.21 StartZ=0 EndX=0.23332 EndY=0.21 EndZ=0
    g8: LineSegment StartX=0 StartY=0.24 StartZ=0 EndX=0.23329 EndY=0.24 EndZ=0
    g9: LineSegment StartX=0 StartY=0.28956 StartZ=0 EndX=0.23334 EndY=0.28956 EndZ=0
    g10: LineSegment StartX=0 StartY=0.27 StartZ=0 EndX=0.23332 EndY=0.27 EndZ=0
  constraints (43):
    c: Coincident(g0,g-1)
    c: PointOnObject(g0,g-1)
    c: PointOnObject(g1,g-2)
    c: Horizontal(g1)
    c: PointOnObject(g2,g-2)
    c: Horizontal(g2)
    c: PointOnObject(g3,g-2)
    c: Horizontal(g3)
    c: PointOnObject(g4,g-2)
    c: Horizontal(g4)
    c: PointOnObject(g5,g-2)
    c: Horizontal(g5)
    c: PointOnObject(g6,g-2)
    c: Horizontal(g6)
    c: PointOnObject(g7,g-2)
    c: Horizontal(g7)
    c: PointOnObject(g8,g-2)
    c: Horizontal(g8)
    c: PointOnObject(g9,g-2)
    c: Horizontal(g9)
    c: DistanceY(g0,g1) = 0.03
    c: DistanceY(g0,g2) = 0.06
    c: DistanceY(g0,g3) = 0.09
    c: DistanceY(g0,g5) = 0.12
    c: DistanceY(g0,g4) = 0.15
    c: DistanceY(g0,g6) = 0.18
    c: DistanceY(g0,g7) = 0.21
    c: DistanceY(g0,g8) = 0.24
    c: DistanceY(g0,g9) = 0.28956
    c: PointOnObject(g10,g-2)
    c: Horizontal(g10)
    c: DistanceY(g0,g10) = 0.27
    c: DistanceX(g9,g9) = 0.23334
    c: DistanceX(g10,g10) = 0.23332
    c: DistanceX(g8,g8) = 0.23329
    c: DistanceX(g7,g7) = 0.23332
    c: DistanceX(g6,g6) = 0.23339
    c: DistanceX(g4,g4) = 0.2335
    c: DistanceX(g5,g5) = 0.23366
    c: DistanceX(g3,g3) = 0.23375
    c: DistanceX(g2,g2) = 0.23305
    c: DistanceX(g1,g1) = 0.22247
    c: DistanceX(g0,g0) = 0.15932
FEATURE [Sketcher::SketchObject] Sketch017
  AttachmentOffset = pos=(0,0,2.38717) rot=(0,0,1;0rad)
  FullyConstrained = true
  MapMode = 5
  Placement = pos=(2.38717,-5e-16,5e-16) rot=(0.57735,0.57735,0.57735;2.0944rad)
  Support = -> [YZ_Plane]
  expr: Constraints[20] = Sketch.Constraints[20]
  expr: Constraints[21] = Sketch.Constraints[21]
  expr: Constraints[22] = Sketch.Constraints[22]
  expr: Constraints[23] = Sketch.Constraints[23]
  expr: Constraints[24] = Sketch.Constraints[24]
  expr: Constraints[25] = Sketch.Constraints[25]
  expr: Constraints[26] = Sketch.Constraints[26]
  expr: Constraints[27] = Sketch.Constraints[27]
  expr: Constraints[28] = Sketch.Constraints[28]
  expr: Constraints[31] = Sketch.Constraints[41]
  sketch-geometry (11):
    g0: LineSegment StartX=0 StartY=0 StartZ=0 EndX=0.13191 EndY=0 EndZ=0
    g1: LineSegment StartX=0 StartY=0.03 StartZ=0 EndX=0.19878 EndY=0.03 EndZ=0
    g2: LineSegment StartX=0 StartY=0.06 StartZ=0 EndX=0.2165 EndY=0.06 EndZ=0
    g3: LineSegment StartX=0 StartY=0.09 StartZ=0 EndX=0.222 EndY=0.09 EndZ=0
    g4: LineSegment StartX=0 StartY=0.15 StartZ=0 EndX=0.22413 EndY=0.15 EndZ=0
    g5: LineSegment StartX=0 StartY=0.12 StartZ=0 EndX=0.22349 EndY=0.12 EndZ=0
    g6: LineSegment StartX=0 StartY=0.18 StartZ=0 EndX=0.22455 EndY=0.18 EndZ=0
    g7: LineSegment StartX=0 StartY=0.21 StartZ=0 EndX=0.22505 EndY=0.21 EndZ=0
    g8: LineSegment StartX=0 StartY=0.24 StartZ=0 EndX=0.22571 EndY=0.24 EndZ=0
    g9: LineSegment StartX=0 StartY=0.28956 StartZ=0 EndX=0.22782 EndY=0.28956 EndZ=0
    g10: LineSegment StartX=0 StartY=0.27 StartZ=0 EndX=0.22683 EndY=0.27 EndZ=0
  constraints (43):
    c: Coincident(g0,g-1)
    c: PointOnObject(g0,g-1)
    c: PointOnObject(g1,g-2)
    c: Horizontal(g1)
    c: PointOnObject(g2,g-2)
    c: Horizontal(g2)
    c: PointOnObject(g3,g-2)
    c: Horizontal(g3)
    c: PointOnObject(g4,g-2)
    c: Horizontal(g4)
    c: PointOnObject(g5,g-2)
    c: Horizontal(g5)
    c: PointOnObject(g6,g-2)
    c: Horizontal(g6)
    c: PointOnObject(g7,g-2)
    c: Horizontal(g7)
    c: PointOnObject(g8,g-2)
    c: Horizontal(g8)
    c: PointOnObject(g9,g-2)
    c: Horizontal(g9)
    c: DistanceY(g0,g1) = 0.03
    c: DistanceY(g0,g2) = 0.06
    c: DistanceY(g0,g3) = 0.09
    c: DistanceY(g0,g5) = 0.12
    c: DistanceY(g0,g4) = 0.15
    c: DistanceY(g0,g6) = 0.18
    c: DistanceY(g0,g7) = 0.21
    c: DistanceY(g0,g8) = 0.24
    c: DistanceY(g0,g9) = 0.28956
    c: PointOnObject(g10,g-2)
    c: Horizontal(g10)
    c: DistanceY(g0,g10) = 0.27
    c: DistanceX(g9,g9) = 0.22782
    c: DistanceX(g10,g10) = 0.22683
    c: DistanceX(g8,g8) = 0.22571
    c: DistanceX(g7,g7) = 0.22505
    c: DistanceX(g6,g6) = 0.22455
    c: DistanceX(g4,g4) = 0.22413
    c: DistanceX(g5,g5) = 0.22349
    c: DistanceX(g3,g3) = 0.222
    c: DistanceX(g2,g2) = 0.2165
    c: DistanceX(g1,g1) = 0.19878
    c: DistanceX(g0,g0) = 0.13191
FEATURE [Sketcher::SketchObject] Sketch018
  AttachmentOffset = pos=(0,0,2.61566) rot=(0,0,1;0rad)
  FullyConstrained = true
  MapMode = 5
  Placement = pos=(2.61566,-6e-16,6e-16) rot=(0.57735,0.57735,0.57735;2.0944rad)
  Support = -> [YZ_Plane]
  expr: Constraints[20] = Sketch.Constraints[20]
  expr: Constraints[21] = Sketch.Constraints[21]
  expr: Constraints[22] = Sketch.Constraints[22]
  expr: Constraints[23] = Sketch.Constraints[23]
  expr: Constraints[24] = Sketch.Constraints[24]
  expr: Constraints[25] = Sketch.Constraints[25]
  expr: Constraints[26] = Sketch.Constraints[26]
  expr: Constraints[27] = Sketch.Constraints[27]
  expr: Constraints[28] = Sketch.Constraints[28]
  expr: Constraints[31] = Sketch.Constraints[41]
  sketch-geometry (11):
    g0: LineSegment StartX=0 StartY=0 StartZ=0 EndX=0.08897 EndY=0 EndZ=0
    g1: LineSegment StartX=0 StartY=0.03 StartZ=0 EndX=0.16667 EndY=0.03 EndZ=0
    g2: LineSegment StartX=0 StartY=0.06 StartZ=0 EndX=0.18833 EndY=0.06 EndZ=0
    g3: LineSegment StartX=0 StartY=0.09 StartZ=0 EndX=0.19773 EndY=0.09 EndZ=0
    g4: LineSegment StartX=0 StartY=0.15 StartZ=0 EndX=0.20282 EndY=0.15 EndZ=0
    g5: LineSegment StartX=0 StartY=0.12 StartZ=0 EndX=0.20107 EndY=0.12 EndZ=0
    g6: LineSegment StartX=0 StartY=0.18 StartZ=0 EndX=0.20475 EndY=0.18 EndZ=0
    g7: LineSegment StartX=0 StartY=0.21 StartZ=0 EndX=0.20705 EndY=0.21 EndZ=0
    g8: LineSegment StartX=0 StartY=0.24 StartZ=0 EndX=0.21038 EndY=0.24 EndZ=0
    g9: LineSegment StartX=0 StartY=0.28956 StartZ=0 EndX=0.21724 EndY=0.28956 EndZ=0
    g10: LineSegment StartX=0 StartY=0.27 StartZ=0 EndX=0.21436 EndY=0.27 EndZ=0
  constraints (43):
    c: Coincident(g0,g-1)
    c: PointOnObject(g0,g-1)
    c: PointOnObject(g1,g-2)
    c: Horizontal(g1)
    c: PointOnObject(g2,g-2)
    c: Horizontal(g2)
    c: PointOnObject(g3,g-2)
    c: Horizontal(g3)
    c: PointOnObject(g4,g-2)
    c: Horizontal(g4)
    c: PointOnObject(g5,g-2)
    c: Horizontal(g5)
    c: PointOnObject(g6,g-2)
    c: Horizontal(g6)
    c: PointOnObject(g7,g-2)
    c: Horizontal(g7)
    c: PointOnObject(g8,g-2)
    c: Horizontal(g8)
    c: PointOnObject(g9,g-2)
    c: Horizontal(g9)
    c: DistanceY(g0,g1) = 0.03
    c: DistanceY(g0,g2) = 0.06
    c: DistanceY(g0,g3) = 0.09
    c: DistanceY(g0,g5) = 0.12
    c: DistanceY(g0,g4) = 0.15
    c: DistanceY(g0,g6) = 0.18
    c: DistanceY(g0,g7) = 0.21
    c: DistanceY(g0,g8) = 0.24
    c: DistanceY(g0,g9) = 0.28956
    c: PointOnObject(g10,g-2)
    c: Horizontal(g10)
    c: DistanceY(g0,g10) = 0.27
    c: DistanceX(g9,g9) = 0.21724
    c: DistanceX(g10,g10) = 0.21436
    c: DistanceX(g8,g8) = 0.21038
    c: DistanceX(g7,g7) = 0.20705
    c: DistanceX(g6,g6) = 0.20475
    c: DistanceX(g4,g4) = 0.20282
    c: DistanceX(g5,g5) = 0.20107
    c: DistanceX(g3,g3) = 0.19773
    c: DistanceX(g2,g2) = 0.18833
    c: DistanceX(g0,g0) = 0.08897
    c: DistanceX(g1,g1) = 0.16667
FEATURE [Sketcher::SketchObject] Sketch019
  AttachmentOffset = pos=(0,0,2.79808) rot=(0,0,1;0rad)
  FullyConstrained = false
  MapMode = 5
  Placement = pos=(2.79808,-6e-16,6e-16) rot=(0.57735,0.57735,0.57735;2.0944rad)
  Support = -> [YZ_Plane]
  sketch-geometry (9):
    g0: LineSegment StartX=0 StartY=0 StartZ=0 EndX=0.05644 EndY=0 EndZ=0
    g1: LineSegment StartX=0 StartY=0.041367 StartZ=0 EndX=0.14474 EndY=0.041367 EndZ=0
    g2: LineSegment StartX=0 StartY=0.08273 StartZ=0 EndX=0.1644 EndY=0.08273 EndZ=0
    g3: LineSegment StartX=0 StartY=0.124095 StartZ=0 EndX=0.172 EndY=0.124095 EndZ=0
    g4: LineSegment StartX=0 StartY=0.165461 StartZ=0 EndX=0.17676 EndY=0.165461 EndZ=0
    g5: LineSegment StartX=0 StartY=0.206825 StartZ=0 EndX=0.18213 EndY=0.206825 EndZ=0
    g6: LineSegment StartX=0 StartY=0.248191 StartZ=0 EndX=0.18911 EndY=0.248191 EndZ=0
    g7: LineSegment StartX=0 StartY=0.28956 StartZ=0 EndX=0.19843 EndY=0.28956 EndZ=0
    g8: LineSegment StartX=0.00043 StartY=0.020683 StartZ=0 EndX=0.121732 EndY=0.020683 EndZ=0
  constraints (33):
    c: Coincident(g0,g-1)
    c: PointOnObject(g0,g-1)
    c: PointOnObject(g1,g-2)
    c: Horizontal(g1)
    c: PointOnObject(g2,g-2)
    c: Horizontal(g2)
    c: PointOnObject(g3,g-2)
    c: Horizontal(g3)
    c: PointOnObject(g4,g-2)
    c: Horizontal(g4)
    c: PointOnObject(g5,g-2)
    c: Horizontal(g5)
    c: PointOnObject(g6,g-2)
    c: Horizontal(g6)
    c: PointOnObject(g7,g-2)
    c: Horizontal(g7)
    c: DistanceY(g0,g1) = 0.041367
    c: DistanceY(g0,g2) = 0.08273
    c: DistanceY(g0,g3) = 0.124095
    c: DistanceY(g0,g4) = 0.165461
    c: DistanceY(g0,g5) = 0.206825
    c: DistanceY(g0,g6) = 0.248191
    c: DistanceY(g0,g7) = 0.28956
    c: DistanceX(g7,g7) = 0.19843
    c: DistanceX(g6,g6) = 0.18911
    c: DistanceX(g5,g5) = 0.18213
    c: DistanceX(g4,g4) = 0.17676
    c: DistanceX(g3,g3) = 0.172
    c: DistanceX(g2,g2) = 0.1644
    c: DistanceX(g1,g1) = 0.14474
    c: DistanceX(g0,g0) = 0.05644
    c: Horizontal(g8)
    c: DistanceY(g0,g8) = 0.020683
FEATURE [Sketcher::SketchObject] Sketch020
  AttachmentOffset = pos=(0,0,2.89808) rot=(0,0,1;0rad)
  FullyConstrained = false
  MapMode = 5
  Placement = pos=(2.89808,-6e-16,6e-16) rot=(0.57735,0.57735,0.57735;2.0944rad)
  Support = -> [YZ_Plane]
  expr: Constraints[14] = Sketch019.Constraints[16]
  expr: Constraints[15] = Sketch019.Constraints[17]
  expr: Constraints[16] = Sketch019.Constraints[18]
  expr: Constraints[17] = Sketch019.Constraints[19]
  expr: Constraints[18] = Sketch019.Constraints[20]
  expr: Constraints[19] = Sketch019.Constraints[21]
  sketch-geometry (44):
    g0: LineSegment StartX=0 StartY=0 StartZ=0 EndX=0.05567 EndY=0 EndZ=0
    g1: LineSegment StartX=0 StartY=0.041367 StartZ=0 EndX=0.12445 EndY=0.041367 EndZ=0
    g2: LineSegment StartX=0 StartY=0.08273 StartZ=0 EndX=0.14368 EndY=0.08273 EndZ=0
    g3: LineSegment StartX=0 StartY=0.124095 StartZ=0 EndX=0.15159 EndY=0.124095 EndZ=0
    g4: LineSegment StartX=0 StartY=0.165461 StartZ=0 EndX=0.15669 EndY=0.165461 EndZ=0
    g5: LineSegment StartX=0 StartY=0.206825 StartZ=0 EndX=0.16281 EndY=0.206825 EndZ=0
    g6: LineSegment StartX=0 StartY=0.248191 StartZ=0 EndX=0.17141 EndY=0.248191 EndZ=0
    g7-g15: GeomPoint x9 (B-spline internal-alignment scaffolding for g16; pole/knot coordinates omitted)
    g16: BSplineCurve PolesCount=11 KnotsCount=9 Degree=3 IsPeriodic=0
    g17-g27: Circle x11 (B-spline internal-alignment scaffolding for g16; pole/knot coordinates omitted)
    g28: BSplineCurve PolesCount=11 KnotsCount=9 Degree=3 IsPeriodic=0
    g29: GeomPoint X=0.17141 Y=0.248191 Z=0
    g30: GeomPoint X=0.162434 Y=0.207033 Z=0
    g31: GeomPoint X=0.156448 Y=0.165531 Z=0
    g32: GeomPoint X=0.15159 Y=0.124095 Z=0
    g33: GeomPoint X=0.14368 Y=0.08273 Z=0
    g34: GeomPoint X=0.12445 Y=0.041367 Z=0
    g35: GeomPoint X=0.05567 Y=0 Z=0
    g36: GeomPoint X=-0.17141 Y=0.248191 Z=0
    g37: GeomPoint X=-0.162834 Y=0.206964 Z=0
    g38: GeomPoint X=-0.156695 Y=0.1655 Z=0
    g39: GeomPoint X=-0.15159 Y=0.124095 Z=0
    g40: GeomPoint X=-0.14368 Y=0.08273 Z=0
    g41: GeomPoint X=-0.12445 Y=0.041367 Z=0
    g42: GeomPoint X=-0.05567 Y=0 Z=0
    g43: LineSegment StartX=-0.18362 StartY=0.28956 StartZ=0 EndX=0.18362 EndY=0.28956 EndZ=0
  constraints (68):
    c: Coincident(g0,g-1)
    c: PointOnObject(g0,g-1)
    c: PointOnObject(g1,g-2)
    c: Horizontal(g1)
    c: PointOnObject(g2,g-2)
    c: Horizontal(g2)
    c: PointOnObject(g3,g-2)
    c: Horizontal(g3)
    c: PointOnObject(g4,g-2)
    c: Horizontal(g4)
    c: PointOnObject(g5,g-2)
    c: Horizontal(g5)
    c: PointOnObject(g6,g-2)
    c: Horizontal(g6)
    c: DistanceY(g0,g1) = 0.041367
    c: DistanceY(g0,g2) = 0.08273
    c: DistanceY(g0,g3) = 0.124095
    c: DistanceY(g0,g4) = 0.165461
    c: DistanceY(g0,g5) = 0.206825
    c: DistanceY(g0,g6) = 0.248191
    c: Coincident(g8,g6)
    c: Coincident(g9,g5)
    c: Coincident(g10,g4)
    c: Coincident(g11,g3)
    c: Coincident(g12,g2)
    c: Coincident(g13,g1)
    c: Coincident(g14,g0)
    c: Coincident(g16,g0)
    c: InternalAlignment(g7-g15 -> g16) x9
    c: InternalAlignment(g17,g16)
    c: Weight(g17) = 1
    c: InternalAlignment(g18,g16)
    c: Equal(g18,g17)
    c: InternalAlignment(g19,g16)
    c: Equal(g19,g17)
    c: InternalAlignment(g20,g16)
    c: Equal(g20,g17)
    c: InternalAlignment(g21,g16)
    c: Equal(g21,g17)
    c: InternalAlignment(g22,g16)
    c: Equal(g22,g17)
    c: InternalAlignment(g23,g16)
    c: Equal(g23,g17)
    c: InternalAlignment(g24,g16)
    c: Equal(g24,g17)
    c: InternalAlignment(g25,g16)
    c: Equal(g25,g17)
    c: InternalAlignment(g26,g16)
    c: Equal(g26,g17)
    c: InternalAlignment(g27,g16)
    c: Equal(g27,g17)
    c: Coincident(g29,g6)
    c: Coincident(g30,g20)
    c: Coincident(g31,g21)
    c: Coincident(g32,g3)
    c: Coincident(g33,g2)
    c: Coincident(g34,g1)
    c: Coincident(g35,g0)
    c: PointOnObject(g36,g28)
    c: PointOnObject(g37,g28)
    c: PointOnObject(g38,g28)
    c: PointOnObject(g39,g28)
    c: PointOnObject(g40,g28)
    c: PointOnObject(g41,g28)
    c: PointOnObject(g42,g28)
    c: Coincident(g43,g28)
    c: Coincident(g43,g16)
    c: Horizontal(g43)
FEATURE [Sketcher::SketchObject] Sketch058
  FullyConstrained = true
  MapMode = 5
  Placement = pos=(0,0,0) rot=(0.57735,0.57735,0.57735;2.0944rad)
  Support = -> [YZ_Plane]
FEATURE [Sketcher::SketchObject] Sketch007
  AttachmentOffset = pos=(0,0,0.1818) rot=(0,0,1;0rad)
  FullyConstrained = false
  MapMode = 5
  Placement = pos=(0.1818,0,0) rot=(0.57735,0.57735,0.57735;2.0944rad)
  Support = -> [YZ_Plane]
  expr: Constraints[20] = Sketch.Constraints[20]
  expr: Constraints[21] = Sketch.Constraints[21]
  expr: Constraints[22] = Sketch.Constraints[22]
  expr: Constraints[23] = Sketch.Constraints[23]
  expr: Constraints[24] = Sketch.Constraints[24]
  expr: Constraints[25] = Sketch.Constraints[25]
  expr: Constraints[26] = Sketch.Constraints[26]
  expr: Constraints[27] = Sketch.Constraints[27]
  expr: Constraints[28] = Sketch.Constraints[28]
  expr: Constraints[31] = Sketch.Constraints[41]
  sketch-geometry (38):
    g0: LineSegment StartX=0 StartY=0 StartZ=0 EndX=2e-16 EndY=0 EndZ=0
    g1: LineSegment StartX=0 StartY=0.03 StartZ=0 EndX=0.00246 EndY=0.03 EndZ=0
    g2: LineSegment StartX=0 StartY=0.06 StartZ=0 EndX=0.00322 EndY=0.06 EndZ=0
    g3: LineSegment StartX=0 StartY=0.09 StartZ=0 EndX=0.00379 EndY=0.09 EndZ=0
    g4: LineSegment StartX=0 StartY=0.15 StartZ=0 EndX=0.00933 EndY=0.15 EndZ=0
    g5: LineSegment StartX=0 StartY=0.12 StartZ=0 EndX=0.00483 EndY=0.12 EndZ=0
    g6: LineSegment StartX=0 StartY=0.18 StartZ=0 EndX=0.04259 EndY=0.18 EndZ=0
    g7: LineSegment StartX=0 StartY=0.21 StartZ=0 EndX=0.086 EndY=0.21 EndZ=0
    g8: LineSegment StartX=0 StartY=0.24 StartZ=0 EndX=0.11034 EndY=0.24 EndZ=0
    g9: LineSegment StartX=0 StartY=0.28956 StartZ=0 EndX=0.1382 EndY=0.28956 EndZ=0
    g10: LineSegment StartX=0 StartY=0.27 StartZ=0 EndX=0.12816 EndY=0.27 EndZ=0
    g11-g21: GeomPoint x11 (B-spline internal-alignment scaffolding for g22; pole/knot coordinates omitted)
    g22: BSplineCurve PolesCount=13 KnotsCount=11 Degree=3 IsPeriodic=0
    g23-g35: Circle x13 (B-spline internal-alignment scaffolding for g22; pole/knot coordinates omitted)
    g36: BSplineCurve PolesCount=13 KnotsCount=11 Degree=3 IsPeriodic=0
    g37: LineSegment StartX=0 StartY=0.28956 StartZ=0 EndX=-0.1382 EndY=0.28956 EndZ=0
  constraints (83):
    c: Coincident(g0,g-1)
    c: PointOnObject(g0,g-1)
    c: PointOnObject(g1,g-2)
    c: Horizontal(g1)
    c: PointOnObject(g2,g-2)
    c: Horizontal(g2)
    c: PointOnObject(g3,g-2)
    c: Horizontal(g3)
    c: PointOnObject(g4,g-2)
    c: Horizontal(g4)
    c: PointOnObject(g5,g-2)
    c: Horizontal(g5)
    c: PointOnObject(g6,g-2)
    c: Horizontal(g6)
    c: PointOnObject(g7,g-2)
    c: Horizontal(g7)
    c: PointOnObject(g8,g-2)
    c: Horizontal(g8)
    c: PointOnObject(g9,g-2)
    c: Horizontal(g9)
    c: DistanceY(g0,g1) = 0.03
    c: DistanceY(g0,g2) = 0.06
    c: DistanceY(g0,g3) = 0.09
    c: DistanceY(g0,g5) = 0.12
    c: DistanceY(g0,g4) = 0.15
    c: DistanceY(g0,g6) = 0.18
    c: DistanceY(g0,g7) = 0.21
    c: DistanceY(g0,g8) = 0.24
    c: DistanceY(g0,g9) = 0.28956
    c: PointOnObject(g10,g-2)
    c: Horizontal(g10)
    c: DistanceY(g0,g10) = 0.27
    c: DistanceX(g9,g9) = 0.1382
    c: DistanceX(g10,g10) = 0.12816
    c: DistanceX(g8,g8) = 0.11034
    c: DistanceX(g7,g7) = 0.086
    c: DistanceX(g6,g6) = 0.04259
    c: DistanceX(g4,g4) = 0.00933
    c: DistanceX(g5,g5) = 0.00483
    c: DistanceX(g3,g3) = 0.00379
    c: DistanceX(g2,g2) = 0.00322
    c: DistanceX(g1,g1) = 0.00246
    c: DistanceX(g0,g0) = 0
    c: Coincident(g22,g9)
    c: Coincident(g12,g10)
    c: Coincident(g13,g8)
    c: Coincident(g14,g7)
    c: Coincident(g15,g6)
    c: Coincident(g16,g4)
    c: Coincident(g17,g5)
    c: Coincident(g18,g3)
    c: Coincident(g19,g2)
    c: Coincident(g20,g1)
    c: Coincident(g22,g0)
    c: InternalAlignment(g11-g21 -> g22) x11
    c: InternalAlignment(g23,g22)
    c: Weight(g23) = 1
    c: InternalAlignment(g24,g22)
    c: Equal(g24,g23)
    c: InternalAlignment(g25,g22)
    c: Equal(g25,g23)
    c: InternalAlignment(g26,g22)
    c: Equal(g26,g23)
    c: InternalAlignment(g27,g22)
    c: Equal(g27,g23)
    c: InternalAlignment(g28,g22)
    c: Equal(g28,g23)
    c: InternalAlignment(g29,g22)
    c: Equal(g29,g23)
    c: InternalAlignment(g30,g22)
    c: Equal(g30,g23)
    c: InternalAlignment(g31,g22)
    c: Equal(g31,g23)
    c: InternalAlignment(g32,g22)
    c: Equal(g32,g23)
    c: InternalAlignment(g33,g22)
    c: Equal(g33,g23)
    c: InternalAlignment(g34,g22)
    c: Equal(g34,g23)
    c: InternalAlignment(g35,g22)
    c: Equal(g35,g23)
    c: Horizontal(g37)
    c: Coincident(g36,g37)
FEATURE [Sketcher::SketchObject] Sketch009
  AttachmentOffset = pos=(0,0,0.04904) rot=(0,0,1;0rad)
  FullyConstrained = false
  MapMode = 5
  Placement = pos=(0.04904,0,0) rot=(0.57735,0.57735,0.57735;2.0944rad)
  Support = -> [YZ_Plane]
  expr: Constraints[11] = Sketch.Constraints[41]
  expr: Constraints[6] = Sketch.Constraints[26]
  expr: Constraints[7] = Sketch.Constraints[27]
  expr: Constraints[8] = Sketch.Constraints[28]
  sketch-geometry (31):
    g0: LineSegment StartX=0 StartY=0.21 StartZ=0 EndX=0.02379 EndY=0.21 EndZ=0
    g1: LineSegment StartX=0 StartY=0.24 StartZ=0 EndX=0.04896 EndY=0.24 EndZ=0
    g2: LineSegment StartX=0 StartY=0.28956 StartZ=0 EndX=0.07704 EndY=0.28956 EndZ=0
    g3: LineSegment StartX=0 StartY=0.27 StartZ=0 EndX=0.06654 EndY=0.27 EndZ=0
    g4: GeomPoint X=0 Y=0.1959 Z=0
    g5: LineSegment StartX=0 StartY=0.21 StartZ=0 EndX=-0.02379 EndY=0.21 EndZ=0
    g6: LineSegment StartX=0 StartY=0.24 StartZ=0 EndX=-0.04896 EndY=0.24 EndZ=0
    g7: LineSegment StartX=0 StartY=0.28956 StartZ=0 EndX=-0.07704 EndY=0.28956 EndZ=0
    g8: LineSegment StartX=0 StartY=0.27 StartZ=0 EndX=-0.06654 EndY=0.27 EndZ=0
    g9: GeomPoint X=0 Y=0.1959 Z=0
    g10-g18: GeomPoint x9 (B-spline internal-alignment scaffolding for g19; pole/knot coordinates omitted)
    g19: BSplineCurve PolesCount=11 KnotsCount=9 Degree=3 IsPeriodic=0
    g20-g30: Circle x11 (B-spline internal-alignment scaffolding for g19; pole/knot coordinates omitted)
  constraints (54):
    c: PointOnObject(g0,g-2)
    c: Horizontal(g0)
    c: PointOnObject(g1,g-2)
    c: Horizontal(g1)
    c: PointOnObject(g2,g-2)
    c: Horizontal(g2)
    c: DistanceY(g-1,g0) = 0.21
    c: DistanceY(g-1,g1) = 0.24
    c: DistanceY(g-1,g2) = 0.28956
    c: PointOnObject(g3,g-2)
    c: Horizontal(g3)
    c: DistanceY(g-1,g3) = 0.27
    c: DistanceX(g2,g2) = 0.07704
    c: DistanceX(g3,g3) = 0.06654
    c: DistanceX(g1,g1) = 0.04896
    c: DistanceX(g0,g0) = 0.02379
    c: PointOnObject(g4,g-2)
    c: DistanceY(g-1,g4) = 0.1959
    c: Horizontal(g5)
    c: Horizontal(g6)
    c: Horizontal(g7)
    c: Horizontal(g8)
    c: Coincident(g19,g2)
    c: Coincident(g11,g3)
    c: Coincident(g12,g1)
    c: Coincident(g13,g0)
    c: Coincident(g14,g4)
    c: Coincident(g15,g5)
    c: Coincident(g16,g6)
    c: Coincident(g17,g8)
    c: Coincident(g19,g7)
    c: InternalAlignment(g10-g18 -> g19) x9
    c: InternalAlignment(g20,g19)
    c: Weight(g20) = 1
    c: InternalAlignment(g21,g19)
    c: Equal(g21,g20)
    c: InternalAlignment(g22,g19)
    c: Equal(g22,g20)
    c: InternalAlignment(g23,g19)
    c: Equal(g23,g20)
    c: InternalAlignment(g24,g19)
    c: Equal(g24,g20)
    c: InternalAlignment(g25,g19)
    c: Equal(g25,g20)
    c: InternalAlignment(g26,g19)
    c: Equal(g26,g20)
    c: InternalAlignment(g27,g19)
    c: Equal(g27,g20)
    c: InternalAlignment(g28,g19)
    c: Equal(g28,g20)
    c: InternalAlignment(g29,g19)
    c: Equal(g29,g20)
    c: InternalAlignment(g30,g19)
    c: Equal(g30,g20)
FEATURE [Sketcher::SketchObject] Sketch010
  FullyConstrained = true
  MapMode = 5
  Placement = pos=(0,0,0) rot=(0.57735,0.57735,0.57735;2.0944rad)
  Support = -> [YZ_Plane]
  sketch-geometry (1):
    g0: GeomPoint X=0 Y=0.28956 Z=0
  constraints (2):
    c: PointOnObject(g0,g-2)
    c: DistanceY(g-1,g0) = 0.28956
FEATURE [Sketcher::SketchObject] Sketch011
  AttachmentOffset = pos=(0,0,0.10904) rot=(0,0,1;0rad)
  FullyConstrained = false
  MapMode = 5
  Placement = pos=(0.10904,0,0) rot=(0.57735,0.57735,0.57735;2.0944rad)
  Support = -> [YZ_Plane]
  expr: Constraints[10] = Sketch.Constraints[27]
  expr: Constraints[11] = Sketch.Constraints[28]
  expr: Constraints[14] = Sketch.Constraints[41]
  expr: Constraints[8] = Sketch.Constraints[25]
  expr: Constraints[9] = Sketch.Constraints[26]
  sketch-geometry (12):
    g0: LineSegment StartX=0 StartY=0.18 StartZ=0 EndX=0.00832 EndY=0.18 EndZ=0
    g1: LineSegment StartX=0 StartY=0.21 StartZ=0 EndX=0.06043 EndY=0.21 EndZ=0
    g2: LineSegment StartX=0 StartY=0.24 StartZ=0 EndX=0.08327 EndY=0.24 EndZ=0
    g3: LineSegment StartX=0 StartY=0.28956 StartZ=0 EndX=0.10981 EndY=0.28956 EndZ=0
    g4: LineSegment StartX=0 StartY=0.27 StartZ=0 EndX=0.09991 EndY=0.27 EndZ=0
    g5: GeomPoint X=0 Y=0.17754 Z=0
    g6: LineSegment StartX=0 StartY=0.18 StartZ=0 EndX=-0.00832 EndY=0.18 EndZ=0
    g7: LineSegment StartX=0 StartY=0.21 StartZ=0 EndX=-0.06043 EndY=0.21 EndZ=0
    g8: LineSegment StartX=0 StartY=0.24 StartZ=0 EndX=-0.08327 EndY=0.24 EndZ=0
    g9: LineSegment StartX=0 StartY=0.28956 StartZ=0 EndX=-0.10981 EndY=0.28956 EndZ=0
    g10: LineSegment StartX=0 StartY=0.27 StartZ=0 EndX=-0.09991 EndY=0.27 EndZ=0
    g11: GeomPoint X=0 Y=0.17754 Z=0
  constraints (27):
    c: PointOnObject(g0,g-2)
    c: Horizontal(g0)
    c: PointOnObject(g1,g-2)
    c: Horizontal(g1)
    c: PointOnObject(g2,g-2)
    c: Horizontal(g2)
    c: PointOnObject(g3,g-2)
    c: Horizontal(g3)
    c: DistanceY(g-1,g0) = 0.18
    c: DistanceY(g-1,g1) = 0.21
    c: DistanceY(g-1,g2) = 0.24
    c: DistanceY(g-1,g3) = 0.28956
    c: PointOnObject(g4,g-2)
    c: Horizontal(g4)
    c: DistanceY(g-1,g4) = 0.27
    c: DistanceX(g3,g3) = 0.10981
    c: DistanceX(g4,g4) = 0.09991
    c: DistanceX(g2,g2) = 0.08327
    c: DistanceX(g1,g1) = 0.06043
    c: DistanceX(g0,g0) = 0.00832
    c: PointOnObject(g5,g-2)
    c: DistanceY(g-1,g5) = 0.17754
    c: Horizontal(g6)
    c: Horizontal(g7)
    c: Horizontal(g8)
    c: Horizontal(g9)
    c: Horizontal(g10)
FEATURE [Sketcher::SketchObject] Sketch014
  AttachmentOffset = pos=(0,0,0.13904) rot=(0,0,1;0rad)
  FullyConstrained = false
  MapMode = 5
  Placement = pos=(0.13904,0,0) rot=(0.57735,0.57735,0.57735;2.0944rad)
  Support = -> [YZ_Plane]
  sketch-geometry (37):
    g0: LineSegment StartX=0 StartY=0.18 StartZ=0 EndX=0.02432 EndY=0.18 EndZ=0
    g1: LineSegment StartX=0 StartY=0.21 StartZ=0 EndX=0.07201 EndY=0.21 EndZ=0
    g2: LineSegment StartX=0 StartY=0.24 StartZ=0 EndX=0.09529 EndY=0.24 EndZ=0
    g3: LineSegment StartX=0 StartY=0.28956 StartZ=0 EndX=0.12235 EndY=0.28956 EndZ=0
    g4: LineSegment StartX=0 StartY=0.27 StartZ=0 EndX=0.11237 EndY=0.27 EndZ=0
    g5: GeomPoint X=0 Y=0.16877 Z=0
    g6: LineSegment StartX=0 StartY=0.18 StartZ=0 EndX=-0.02432 EndY=0.18 EndZ=0
    g7: LineSegment StartX=0 StartY=0.21 StartZ=0 EndX=-0.07201 EndY=0.21 EndZ=0
    g8: LineSegment StartX=0 StartY=0.24 StartZ=0 EndX=-0.09529 EndY=0.24 EndZ=0
    g9: LineSegment StartX=0 StartY=0.28956 StartZ=0 EndX=-0.12235 EndY=0.28956 EndZ=0
    g10: LineSegment StartX=0 StartY=0.27 StartZ=0 EndX=-0.11237 EndY=0.27 EndZ=0
    g11: GeomPoint X=0 Y=0.16877 Z=0
    g12-g22: GeomPoint x11 (B-spline internal-alignment scaffolding for g23; pole/knot coordinates omitted)
    g23: BSplineCurve PolesCount=13 KnotsCount=11 Degree=3 IsPeriodic=0
    g24-g36: Circle x13 (B-spline internal-alignment scaffolding for g23; pole/knot coordinates omitted)
  constraints (60):
    c: PointOnObject(g0,g-2)
    c: Horizontal(g0)
    c: PointOnObject(g1,g-2)
    c: Horizontal(g1)
    c: PointOnObject(g2,g-2)
    c: Horizontal(g2)
    c: PointOnObject(g3,g-2)
    c: Horizontal(g3)
    c: PointOnObject(g4,g-2)
    c: Horizontal(g4)
    c: DistanceX(g3,g3) = 0.12235
    c: DistanceX(g4,g4) = 0.11237
    c: DistanceX(g2,g2) = 0.09529
    c: DistanceX(g1,g1) = 0.07201
    c: DistanceX(g0,g0) = 0.02432
    c: PointOnObject(g5,g-2)
    c: DistanceY(g-1,g5) = 0.16877
    c: Horizontal(g6)
    c: Horizontal(g7)
    c: Horizontal(g8)
    c: Horizontal(g9)
    c: Horizontal(g10)
    c: Coincident(g23,g3)
    c: Coincident(g13,g4)
    c: Coincident(g14,g2)
    c: Coincident(g15,g1)
    c: Coincident(g16,g0)
    c: Coincident(g17,g5)
    c: Coincident(g18,g6)
    c: Coincident(g19,g7)
    c: Coincident(g20,g8)
    c: Coincident(g21,g10)
    c: Coincident(g23,g9)
    c: InternalAlignment(g12-g22 -> g23) x11
    c: InternalAlignment(g24,g23)
    c: Weight(g24) = 1
    c: InternalAlignment(g25,g23)
    c: Equal(g25,g24)
    c: InternalAlignment(g26,g23)
    c: Equal(g26,g24)
    c: InternalAlignment(g27,g23)
    c: Equal(g27,g24)
    c: InternalAlignment(g28,g23)
    c: Equal(g28,g24)
    c: InternalAlignment(g29,g23)
    c: Equal(g29,g24)
    c: InternalAlignment(g30,g23)
    c: Equal(g30,g24)
    c: InternalAlignment(g31,g23)
    c: Equal(g31,g24)
    c: InternalAlignment(g32,g23)
    c: Equal(g32,g24)
    c: InternalAlignment(g33,g23)
    c: Equal(g33,g24)
    c: InternalAlignment(g34,g23)
    c: Equal(g34,g24)
    c: InternalAlignment(g35,g23)
    c: Equal(g35,g24)
    c: InternalAlignment(g36,g23)
    c: Equal(g36,g24)
FEATURE [Sketcher::SketchObject] Sketch023
  AttachmentOffset = pos=(0,0,3.09808) rot=(0,0,1;0rad)
  FullyConstrained = false
  MapMode = 5
  Placement = pos=(3.09808,-7e-16,7e-16) rot=(0.57735,0.57735,0.57735;2.0944rad)
  Support = -> [YZ_Plane]
  expr: Constraints[14] = Sketch019.Constraints[16]
  expr: Constraints[15] = Sketch019.Constraints[17]
  expr: Constraints[16] = Sketch019.Constraints[18]
  expr: Constraints[17] = Sketch019.Constraints[19]
  expr: Constraints[18] = Sketch019.Constraints[20]
  expr: Constraints[19] = Sketch019.Constraints[21]
  sketch-geometry (8):
    g0: LineSegment StartX=0 StartY=-2.97e-13 StartZ=0 EndX=0.018981 EndY=-4e-16 EndZ=0
    g1: LineSegment StartX=-2.4e-15 StartY=0.041367 StartZ=0 EndX=0.09 EndY=0.041367 EndZ=0
    g2: LineSegment StartX=-8e-16 StartY=0.08273 StartZ=0 EndX=0.1 EndY=0.08273 EndZ=0
    g3: LineSegment StartX=0 StartY=0.124095 StartZ=0 EndX=0.105226 EndY=0.124095 EndZ=0
    g4: LineSegment StartX=0 StartY=0.165461 StartZ=0 EndX=0.110965 EndY=0.165461 EndZ=0
    g5: LineSegment StartX=0 StartY=0.206825 StartZ=0 EndX=0.117051 EndY=0.206825 EndZ=0
    g6: LineSegment StartX=-1.8e-15 StartY=0.248191 StartZ=0 EndX=0.12733 EndY=0.248191 EndZ=0
    g7: LineSegment StartX=0.14534 StartY=0.28956 StartZ=0 EndX=0 EndY=0.289655 EndZ=0
  constraints (23):
    c: Coincident(g0,g-1)
    c: PointOnObject(g0,g-1)
    c: PointOnObject(g1,g-2)
    c: Horizontal(g1)
    c: PointOnObject(g2,g-2)
    c: Horizontal(g2)
    c: PointOnObject(g3,g-2)
    c: Horizontal(g3)
    c: PointOnObject(g4,g-2)
    c: Horizontal(g4)
    c: PointOnObject(g5,g-2)
    c: Horizontal(g5)
    c: PointOnObject(g6,g-2)
    c: Horizontal(g6)
    c: DistanceY(g0,g1) = 0.041367
    c: DistanceY(g0,g2) = 0.08273
    c: DistanceY(g0,g3) = 0.124095
    c: DistanceY(g0,g4) = 0.165461
    c: DistanceY(g0,g5) = 0.206825
    c: DistanceY(g0,g6) = 0.248191
    c: DistanceX(g6,g6) = 0.12733
    c: DistanceX(g2,g2) = 0.1  'myhull_c2'
    c: DistanceX(g1,g1) = 0.09  'myhull_c1'
FEATURE [Sketcher::SketchObject] Sketch026
  AttachmentOffset = pos=(0,0,3.39808) rot=(0,0,1;0rad)
  FullyConstrained = false
  MapMode = 5
  Placement = pos=(3.39808,-8e-16,8e-16) rot=(0.57735,0.57735,0.57735;2.0944rad)
  Support = -> [YZ_Plane]
  expr: Constraints[12] = Sketch019.Constraints[16]
  expr: Constraints[13] = Sketch019.Constraints[17]
  expr: Constraints[14] = Sketch019.Constraints[18]
  expr: Constraints[15] = Sketch019.Constraints[19]
  expr: Constraints[16] = Sketch019.Constraints[20]
  expr: Constraints[17] = Sketch019.Constraints[21]
  sketch-geometry (29):
    g0: LineSegment StartX=0 StartY=0.041367 StartZ=0 EndX=0.044 EndY=0.041367 EndZ=0
    g1: LineSegment StartX=0 StartY=0.08273 StartZ=0 EndX=0.05 EndY=0.08273 EndZ=0
    g2: LineSegment StartX=0 StartY=0.124095 StartZ=0 EndX=0.04351 EndY=0.124095 EndZ=0
    g3: LineSegment StartX=0 StartY=0.165461 StartZ=0 EndX=0.0434197 EndY=0.165461 EndZ=0
    g4: LineSegment StartX=0 StartY=0.206825 StartZ=0 EndX=0.04704 EndY=0.206825 EndZ=0
    g5: LineSegment StartX=0 StartY=0.248191 StartZ=0 EndX=0.05656 EndY=0.248191 EndZ=0
    g6: LineSegment StartX=0 StartY=0 StartZ=0 EndX=0.00182746 EndY=0 EndZ=0
    g7: LineSegment StartX=0.07379 StartY=0.28956 StartZ=0 EndX=0 EndY=0.28956 EndZ=0
    g8-g16: GeomPoint x9 (B-spline internal-alignment scaffolding for g17; pole/knot coordinates omitted)
    g17: BSplineCurve PolesCount=11 KnotsCount=9 Degree=3 IsPeriodic=0
    g18-g28: Circle x11 (B-spline internal-alignment scaffolding for g17; pole/knot coordinates omitted)
  constraints (57):
    c: PointOnObject(g0,g-2)
    c: Horizontal(g0)
    c: PointOnObject(g1,g-2)
    c: Horizontal(g1)
    c: PointOnObject(g2,g-2)
    c: Horizontal(g2)
    c: PointOnObject(g3,g-2)
    c: Horizontal(g3)
    c: PointOnObject(g4,g-2)
    c: Horizontal(g4)
    c: PointOnObject(g5,g-2)
    c: Horizontal(g5)
    c: DistanceY(g-1,g0) = 0.041367
    c: DistanceY(g-1,g1) = 0.08273
    c: DistanceY(g-1,g2) = 0.124095
    c: DistanceY(g-1,g3) = 0.165461
    c: DistanceY(g-1,g4) = 0.206825
    c: DistanceY(g-1,g5) = 0.248191
    c: DistanceX(g5,g5) = 0.05656
    c: DistanceX(g0,g0) = 0.044  'myhull_b1'
    c: Coincident(g6,g-1)
    c: PointOnObject(g6,g-1)
    c: PointOnObject(g7,g-2)
    c: Horizontal(g7)
    c: DistanceX(g1,g1) = 0.05  'myhull_b2'
    c: Coincident(g17,g7)
    c: Coincident(g9,g5)
    c: Coincident(g10,g4)
    c: Coincident(g11,g3)
    c: Coincident(g12,g2)
    c: Coincident(g13,g1)
    c: Coincident(g14,g0)
    c: Coincident(g15,g6)
    c: Coincident(g17,g6)
    c: InternalAlignment(g8-g16 -> g17) x9
    c: InternalAlignment(g18,g17)
    c: Weight(g18) = 1
    c: InternalAlignment(g19,g17)
    c: Equal(g19,g18)
    c: InternalAlignment(g20,g17)
    c: Equal(g20,g18)
    c: InternalAlignment(g21,g17)
    c: Equal(g21,g18)
    c: InternalAlignment(g22,g17)
    c: Equal(g22,g18)
    c: InternalAlignment(g23,g17)
    c: Equal(g23,g18)
    c: InternalAlignment(g24,g17)
    c: Equal(g24,g18)
    c: InternalAlignment(g25,g17)
    c: Equal(g25,g18)
    c: InternalAlignment(g26,g17)
    c: Equal(g26,g18)
    c: InternalAlignment(g27,g17)
    c: Equal(g27,g18)
    c: InternalAlignment(g28,g17)
    c: Equal(g28,g18)
FEATURE [Sketcher::SketchObject] Sketch028
  AttachmentOffset = pos=(0,0,3.59808) rot=(0,0,1;0rad)
  FullyConstrained = false
  MapMode = 5
  Placement = pos=(3.59808,-8e-16,8e-16) rot=(0.57735,0.57735,0.57735;2.0944rad)
  Support = -> [YZ_Plane]
  expr: Constraints[14] = Sketch019.Constraints[16]
  expr: Constraints[15] = Sketch019.Constraints[17]
  expr: Constraints[16] = Sketch019.Constraints[18]
  expr: Constraints[17] = Sketch019.Constraints[19]
  expr: Constraints[18] = Sketch019.Constraints[20]
  expr: Constraints[19] = Sketch019.Constraints[21]
  sketch-geometry (31):
    g0: LineSegment StartX=0 StartY=0 StartZ=0 EndX=0.000501502 EndY=0 EndZ=0
    g1: LineSegment StartX=0 StartY=0.041367 StartZ=0 EndX=0.015786 EndY=0.041367 EndZ=0
    g2: LineSegment StartX=0 StartY=0.08273 StartZ=0 EndX=0.01838 EndY=0.08273 EndZ=0
    g3: LineSegment StartX=0 StartY=0.124095 StartZ=0 EndX=0.01195 EndY=0.124095 EndZ=0
    g4: LineSegment StartX=0 StartY=0.165461 StartZ=0 EndX=0.0104393 EndY=0.165461 EndZ=0
    g5: LineSegment StartX=0 StartY=0.206825 StartZ=0 EndX=0.01269 EndY=0.206825 EndZ=0
    g6: LineSegment StartX=0 StartY=0.248191 StartZ=0 EndX=0.01888 EndY=0.248191 EndZ=0
    g7: LineSegment StartX=0 StartY=0 StartZ=0 EndX=2e-16 EndY=0 EndZ=0
    g8: GeomPoint X=0 Y=0 Z=0
    g9: LineSegment StartX=0 StartY=0.28956 StartZ=0 EndX=0.02822 EndY=0.28956 EndZ=0
    g10-g18: GeomPoint x9 (B-spline internal-alignment scaffolding for g19; pole/knot coordinates omitted)
    g19: BSplineCurve PolesCount=11 KnotsCount=9 Degree=3 IsPeriodic=0
    g20-g30: Circle x11 (B-spline internal-alignment scaffolding for g19; pole/knot coordinates omitted)
  constraints (56):
    c: Coincident(g0,g-1)
    c: PointOnObject(g0,g-1)
    c: PointOnObject(g1,g-2)
    c: Horizontal(g1)
    c: PointOnObject(g2,g-2)
    c: Horizontal(g2)
    c: PointOnObject(g3,g-2)
    c: Horizontal(g3)
    c: PointOnObject(g4,g-2)
    c: Horizontal(g4)
    c: PointOnObject(g5,g-2)
    c: Horizontal(g5)
    c: PointOnObject(g6,g-2)
    c: Horizontal(g6)
    c: DistanceY(g0,g1) = 0.041367
    c: DistanceY(g0,g2) = 0.08273
    c: DistanceY(g0,g3) = 0.124095
    c: DistanceY(g0,g4) = 0.165461
    c: DistanceY(g0,g5) = 0.206825
    c: DistanceY(g0,g6) = 0.248191
    c: DistanceX(g6,g6) = 0.01888
    c: DistanceX(g1,g1) = 0.015786  'myhull_a1'
    c: Horizontal(g9)
    c: DistanceX(g2,g2) = 0.01838  'myhull_a2'
    c: Coincident(g19,g9)
    c: Coincident(g11,g6)
    c: Coincident(g12,g5)
    c: Coincident(g13,g4)
    c: Coincident(g14,g3)
    c: Coincident(g15,g2)
    c: Coincident(g16,g1)
    c: Coincident(g17,g0)
    c: Coincident(g19,g0)
    c: InternalAlignment(g10-g18 -> g19) x9
    c: InternalAlignment(g20,g19)
    c: Weight(g20) = 1
    c: InternalAlignment(g21,g19)
    c: Equal(g21,g20)
    c: InternalAlignment(g22,g19)
    c: Equal(g22,g20)
    c: InternalAlignment(g23,g19)
    c: Equal(g23,g20)
    c: InternalAlignment(g24,g19)
    c: Equal(g24,g20)
    c: InternalAlignment(g25,g19)
    c: Equal(g25,g20)
    c: InternalAlignment(g26,g19)
    c: Equal(g26,g20)
    c: InternalAlignment(g27,g19)
    c: Equal(g27,g20)
    c: InternalAlignment(g28,g19)
    c: Equal(g28,g20)
    c: InternalAlignment(g29,g19)
    c: Equal(g29,g20)
    c: InternalAlignment(g30,g19)
    c: Equal(g30,g20)
FEATURE [Sketcher::SketchObject] Sketch042
  AttachmentOffset = pos=(0,0,0.28956) rot=(0,0,1;0rad)
  ExternalGeometry = -> [Sketch028,Sketch023]
  FullyConstrained = false
  MapMode = 5
  Placement = pos=(0,0,0.28956) rot=(0,0,1;0rad)
  Support = -> [XY_Plane]
  sketch-geometry (27):
    g0: LineSegment StartX=2.89808 StartY=-0.18362 StartZ=0 EndX=2.89808 EndY=0.18362 EndZ=0
    g1-g5: GeomPoint x5 (B-spline internal-alignment scaffolding for g6; pole/knot coordinates omitted)
    g6: BSplineCurve PolesCount=7 KnotsCount=5 Degree=3 IsPeriodic=0
    g7-g13: Circle x7 (B-spline internal-alignment scaffolding for g6; pole/knot coordinates omitted)
    g14-g18: GeomPoint x5 (B-spline internal-alignment scaffolding for g19; pole/knot coordinates omitted)
    g19: BSplineCurve PolesCount=7 KnotsCount=5 Degree=3 IsPeriodic=0
    g20-g26: Circle x7 (B-spline internal-alignment scaffolding for g19; pole/knot coordinates omitted)
  constraints (33):
    c: Coincident(g6,g0)
    c: InternalAlignment(g1-g5 -> g6) x5
    c: InternalAlignment(g7,g6)
    c: Weight(g7) = 1
    c: InternalAlignment(g8,g6)
    c: Equal(g8,g7)
    c: InternalAlignment(g9,g6)
    c: Equal(g9,g7)
    c: InternalAlignment(g10,g6)
    c: Equal(g10,g7)
    c: InternalAlignment(g11,g6)
    c: Equal(g11,g7)
    c: InternalAlignment(g12,g6)
    c: Equal(g12,g7)
    c: InternalAlignment(g13,g6)
    c: Equal(g13,g7)
    c: Coincident(g19,g6)
    c: Coincident(g19,g0)
    c: InternalAlignment(g14-g18 -> g19) x5
    c: InternalAlignment(g20,g19)
    c: Weight(g20) = 1
    c: InternalAlignment(g21,g19)
    c: Equal(g21,g20)
    c: InternalAlignment(g22,g19)
    c: Equal(g22,g20)
    c: InternalAlignment(g23,g19)
    c: Equal(g23,g20)
    c: InternalAlignment(g24,g19)
    c: Equal(g24,g20)
    c: InternalAlignment(g25,g19)
    c: Equal(g25,g20)
    c: InternalAlignment(g26,g19)
    c: Equal(g26,g20)
FEATURE [Sketcher::SketchObject] Sketch029
  ExternalGeometry = -> [Sketch019,Sketch042]
  FullyConstrained = false
  MapMode = 5
  Placement = pos=(0,0,0) rot=(1,0,0;1.5708rad)
  Support = -> [XZ_Plane]
  sketch-geometry (19):
    g0: GeomPoint X=3.65 Y=0.02887 Z=0
    g1: GeomPoint X=3.68 Y=0.12 Z=0
    g2: GeomPoint X=3.69 Y=0.21 Z=0
    g3: LineSegment StartX=3.65 StartY=0.02887 StartZ=0 EndX=2.8 EndY=0.02887 EndZ=0
    g4: LineSegment StartX=3.68 StartY=0.12 StartZ=0 EndX=2.8 EndY=0.12 EndZ=0
    g5: LineSegment StartX=3.69 StartY=0.21 StartZ=0 EndX=2.8 EndY=0.21 EndZ=0
    g6-g10: GeomPoint x5 (B-spline internal-alignment scaffolding for g11; pole/knot coordinates omitted)
    g11: BSplineCurve PolesCount=7 KnotsCount=5 Degree=3 IsPeriodic=0
    g12-g18: Circle x7 (B-spline internal-alignment scaffolding for g11; pole/knot coordinates omitted)
  constraints (31):
    c: Coincident(g3,g0)
    c: Horizontal(g3)
    c: Coincident(g4,g1)
    c: Horizontal(g4)
    c: Coincident(g5,g2)
    c: Horizontal(g5)
    c: DistanceX(g5,g5) = 0.89
    c: DistanceX(g4,g4) = 0.88  'myhull_c2'
    c: DistanceX(g3,g3) = 0.85  'myhull_d1'
    c: DistanceX(g-1,g3) = 2.8
    c: DistanceX(g-1,g4) = 2.8
    c: DistanceX(g-1,g5) = 2.8
    c: Coincident(g7,g2)
    c: Coincident(g8,g1)
    c: Coincident(g9,g0)
    c: InternalAlignment(g6-g10 -> g11) x5
    c: InternalAlignment(g12,g11)
    c: Weight(g12) = 1
    c: InternalAlignment(g13,g11)
    c: Equal(g13,g12)
    c: InternalAlignment(g14,g11)
    c: Equal(g14,g12)
    c: InternalAlignment(g15,g11)
    c: Equal(g15,g12)
    c: InternalAlignment(g16,g11)
    c: Equal(g16,g12)
    c: InternalAlignment(g17,g11)
    c: Equal(g17,g12)
    c: InternalAlignment(g18,g11)
    c: Equal(g18,g12)
    c: Coincident(g11,g-4)
FEATURE [Sketcher::SketchObject] Sketch050
  FullyConstrained = true
  MapMode = 5
  Support = -> [XY_Plane]
FEATURE [Sketcher::SketchObject] Sketch052
  AttachmentOffset = pos=(0,0,0.28956) rot=(0,0,1;0rad)
  ExternalGeometry = -> [Sketch020]
  FullyConstrained = true
  MapMode = 5
  Placement = pos=(0,0,0.28956) rot=(0,0,1;0rad)
  Support = -> [XY_Plane]
FEATURE [Sketcher::SketchObject] Sketch055
  AttachmentOffset = pos=(0,0,0.28956) rot=(0,0,1;0rad)
  ExternalGeometry = -> [Sketch023]
  FullyConstrained = false
  MapMode = 5
  Placement = pos=(0,0,0.28956) rot=(0,0,1;0rad)
  Support = -> [XY_Plane]
  sketch-geometry (1):
    g0: LineSegment StartX=3.09808 StartY=0 StartZ=0 EndX=3.39808 EndY=0 EndZ=0
FEATURE [Sketcher::SketchObject] Sketch057
  AttachmentOffset = pos=(0,0,0.28956) rot=(0,0,1;0rad)
  ExternalGeometry = -> [Sketch028,Sketch029]
  FullyConstrained = false
  MapMode = 5
  Placement = pos=(0,0,0.28956) rot=(0,0,1;0rad)
  Support = -> [XY_Plane]
  sketch-geometry (2):
    g0: LineSegment StartX=3.59808 StartY=0.02822 StartZ=0 EndX=3.69564 EndY=0 EndZ=0
    g1: LineSegment StartX=3.59808 StartY=-0.02822 StartZ=0 EndX=3.69564 EndY=0 EndZ=0
  constraints (1):
    c: Coincident(g1,g0)
FEATURE [Sketcher::SketchObject] Sketch060
  AttachmentOffset = pos=(0,0,2.898) rot=(0,0,1;0rad)
  FullyConstrained = false
  MapMode = 5
  Placement = pos=(2.898,-6e-16,6e-16) rot=(0.57735,0.57735,0.57735;2.0944rad)
  Support = -> [YZ_Plane]
  expr: Constraints[14] = Sketch020.Constraints[14]
  expr: Constraints[15] = Sketch020.Constraints[15]
  expr: Constraints[16] = Sketch020.Constraints[16]
  expr: Constraints[17] = Sketch020.Constraints[17]
  expr: Constraints[18] = Sketch020.Constraints[18]
  expr: Constraints[19] = Sketch020.Constraints[19]
  sketch-geometry (8):
    g0: LineSegment StartX=0 StartY=0 StartZ=0 EndX=0.05567 EndY=0 EndZ=0
    g1: LineSegment StartX=0 StartY=0.041367 StartZ=0 EndX=0.12445 EndY=0.041367 EndZ=0
    g2: LineSegment StartX=0 StartY=0.08273 StartZ=0 EndX=0.14368 EndY=0.08273 EndZ=0
    g3: LineSegment StartX=0 StartY=0.124095 StartZ=0 EndX=0.15159 EndY=0.124095 EndZ=0
    g4: LineSegment StartX=0 StartY=0.165461 StartZ=0 EndX=0.15669 EndY=0.165461 EndZ=0
    g5: LineSegment StartX=0 StartY=0.206825 StartZ=0 EndX=0.16281 EndY=0.206825 EndZ=0
    g6: LineSegment StartX=0 StartY=0.248191 StartZ=0 EndX=0.17141 EndY=0.248191 EndZ=0
    g7: LineSegment StartX=0 StartY=0.28956 StartZ=0 EndX=0.18362 EndY=0.28956 EndZ=0
  constraints (20):
    c: Coincident(g0,g-1)
    c: PointOnObject(g0,g-1)
    c: PointOnObject(g1,g-2)
    c: Horizontal(g1)
    c: PointOnObject(g2,g-2)
    c: Horizontal(g2)
    c: PointOnObject(g3,g-2)
    c: Horizontal(g3)
    c: PointOnObject(g4,g-2)
    c: Horizontal(g4)
    c: PointOnObject(g5,g-2)
    c: Horizontal(g5)
    c: PointOnObject(g6,g-2)
    c: Horizontal(g6)
    c: DistanceY(g0,g1) = 0.041367
    c: DistanceY(g0,g2) = 0.08273
    c: DistanceY(g0,g3) = 0.124095
    c: DistanceY(g0,g4) = 0.165461
    c: DistanceY(g0,g5) = 0.206825
    c: DistanceY(g0,g6) = 0.248191
FEATURE [Part::FeaturePython] Interpolation_Curve001  # WARN: FeaturePython — macro-defined, semantics opaque (R4)
  CustomTangents = false
  DetectAligned = false
  Parameters = [0,0.0639228,0.167314,0.281802,0.416796,0.544918,0.638831,0.72691,0.814194,0.901802,1]
  Parametrization = 0
  Periodic = false
  PointList = -> [Sketch006]
  Polygonal = false
  StartOffset = 0
  Tangents = (11) [(0,-0.432101,-0.901825),(2.43768e-15,-0.490269,-0.871571),(2.50581e-16,-0.590396,-0.807113),(-7.43164e-16,-0.710636,-0.70356),(0,-0.797363,-0.6035),+6 more]
  Tolerance = 1e-07
  UTurns = 0
  VTurns = 0
  WireOutput = false
FEATURE [Part::FeaturePython] Interpolation_Curve002  # WARN: FeaturePython — macro-defined, semantics opaque (R4)
  CustomTangents = false
  DetectAligned = false
  Parameters = [0,0.0567577,0.140174,0.231446,0.329316,0.430243,0.528314,0.618437,0.704397,0.793435,0.943128,1]
  Parametrization = 0
  Periodic = false
  PointList = -> [Sketch005]
  Polygonal = false
  StartOffset = 0
  Tangents = (12) [(0,-0.501882,-0.864936),(0,-0.307523,-0.951541),(0,-0.362366,-0.932036),(2.93475e-15,-0.553858,-0.832611),(-2.78099e-15,-0.601102,-0.799172),+7 more]
  Tolerance = 1e-07
  UTurns = 0
  VTurns = 0
  WireOutput = false
FEATURE [Part::FeaturePython] Interpolation_Curve003  # WARN: FeaturePython — macro-defined, semantics opaque (R4)
  CustomTangents = false
  DetectAligned = false
  Parameters = [0,0.0470448,0.119614,0.192998,0.267471,0.343188,0.421066,0.500799,0.582924,0.674626,0.853923,1]
  Parametrization = 0
  Periodic = false
  PointList = -> [Sketch004]
  Polygonal = false
  StartOffset = 0
  Tangents = (12) [(-1.69155e-14,-0.101689,-0.994816),(1.65711e-15,-0.131372,-0.991333),(5.25711e-15,-0.185159,-0.982709),(-3.73962e-15,-0.245086,-0.969501),+8 more]
  Tolerance = 1e-07
  UTurns = 0
  VTurns = 0
  WireOutput = false
FEATURE [Part::FeaturePython] Interpolation_Curve004  # WARN: FeaturePython — macro-defined, semantics opaque (R4)
  CustomTangents = false
  DetectAligned = false
  Parameters = [0,0.0431783,0.109404,0.175651,0.242026,0.308747,0.37613,0.444529,0.515535,0.598336,0.799111,1]
  Parametrization = 0
  Periodic = false
  PointList = -> [Sketch003]
  Polygonal = false
  StartOffset = 0
  Tangents = (12) [(3.40428e-14,-0.0297838,-0.999556),(-1.1188e-14,-0.0274176,-0.999624),(5.65295e-15,-0.0306745,-0.999529),(-4.8756e-17,-0.0517569,-0.99866),+8 more]
  Tolerance = 1e-07
  UTurns = 0
  VTurns = 0
  WireOutput = false
FEATURE [Part::FeaturePython] Interpolation_Curve005  # WARN: FeaturePython — macro-defined, semantics opaque (R4)
  CustomTangents = false
  DetectAligned = false
  Parameters = [0,0.0407743,0.103312,0.165849,0.228385,0.290921,0.353459,0.416108,0.479709,0.551671,0.693823,1]
  Parametrization = 0
  Periodic = false
  PointList = -> [Sketch002]
  Polygonal = false
  StartOffset = 0
  Tangents = (12) [(0,-0.00559613,-0.999984),(0,-0.00558419,-0.999984),(0,-0.00599452,-0.999982),(3.70071e-15,-0.00443717,-0.99999),(-3.70085e-15,-0.00125633,-0.999999),+7 more]
  Tolerance = 1e-07
  UTurns = 0
  VTurns = 0
  WireOutput = false
FEATURE [Part::FeaturePython] Interpolation_Curve006  # WARN: FeaturePython — macro-defined, semantics opaque (R4)
  CustomTangents = false
  DetectAligned = false
  Parameters = [0,0.0398685,0.101016,0.162164,0.223312,0.284461,0.34561,0.406758,0.467922,0.532761,0.675264,1]
  Parametrization = 0
  Periodic = false
  PointList = -> [Sketch001]
  Polygonal = false
  StartOffset = 0
  Tangents = (12) [(0,-0.000630755,-1),(9.66336e-15,-0.00129924,-0.999999),(-4.67197e-15,-0.000153414,-1),(-7.40151e-15,0.00191292,-0.999998),+8 more]
  Tolerance = 1e-07
  UTurns = 0
  VTurns = 0
  WireOutput = false
FEATURE [Part::FeaturePython] Interpolation_Curve007  # WARN: FeaturePython — macro-defined, semantics opaque (R4)
  CustomTangents = false
  DetectAligned = false
  Parameters = [0,0.0396987,0.100586,0.161474,0.222361,0.283249,0.344137,0.405024,0.465912,0.529428,0.659638,1]
  Parametrization = 0
  Periodic = false
  PointList = -> [Sketch]
  Polygonal = false
  StartOffset = 0
  Tangents = (12) [(0,0,-1),(4.83169e-15,6.65572e-06,-1),(-7.88707e-15,-3.37275e-05,-1),(3.70081e-15,0.000128258,-1),(0,-0.000479259,-1),+7 more]
  Tolerance = 1e-07
  UTurns = 0
  VTurns = 0
  WireOutput = false
FEATURE [Part::FeaturePython] Interpolation_Curve008  # WARN: FeaturePython — macro-defined, semantics opaque (R4)
  CustomTangents = false
  DetectAligned = false
  Parameters = [0,0.0398685,0.101016,0.162164,0.223312,0.284461,0.34561,0.406758,0.467922,0.532761,0.675264,1]
  Parametrization = 0
  Periodic = false
  PointList = -> [Sketch016]
  Polygonal = false
  StartOffset = 0
  Tangents = (12) [(0,-0.000630755,-1),(9.66336e-15,-0.00129924,-0.999999),(-8.3727e-15,-0.000153414,-1),(-7.40152e-15,0.00191292,-0.999998),+8 more]
  Tolerance = 1e-07
  UTurns = 0
  VTurns = 0
  WireOutput = false
FEATURE [Part::FeaturePython] Interpolation_Curve009  # WARN: FeaturePython — macro-defined, semantics opaque (R4)
  CustomTangents = false
  DetectAligned = false
  Parameters = [0,0.0416519,0.105498,0.169315,0.233125,0.296933,0.360749,0.42463,0.489494,0.563595,0.719464,1]
  Parametrization = 0
  Periodic = false
  PointList = -> [Sketch017]
  Polygonal = false
  StartOffset = 0
  Tangents = (12) [(0,-0.0559209,-0.998435),(1.62533e-14,-0.0454215,-0.998968),(-7.40053e-15,-0.0285602,-0.999592),(2.23886e-18,-0.018239,-0.999834),+8 more]
  Tolerance = 1e-07
  UTurns = 0
  VTurns = 0
  WireOutput = false
FEATURE [Part::FeaturePython] Interpolation_Curve010  # WARN: FeaturePython — macro-defined, semantics opaque (R4)
  CustomTangents = false
  DetectAligned = false
  Parameters = [0,0.044801,0.113377,0.181774,0.249954,0.318075,0.386171,0.454571,0.52581,0.609657,0.798393,1]
  Parametrization = 0
  Periodic = false
  PointList = -> [Sketch018]
  Polygonal = false
  StartOffset = 0
  Tangents = (12) [(0,-0.150432,-0.98862),(-1.90857e-14,-0.140273,-0.990113),(2.39517e-14,-0.123223,-0.992379),(-3.98776e-17,-0.0922905,-0.995732),+8 more]
  Tolerance = 1e-07
  UTurns = 0
  VTurns = 0
  WireOutput = false
FEATURE [Part::FeaturePython] Interpolation_Curve018  # WARN: FeaturePython — macro-defined, semantics opaque (R4)
  CustomTangents = false
  DetectAligned = false
  Parameters = [0,0.103552,0.205993,0.307849,0.409529,0.51223,0.624065,0.862177,1]
  Parametrization = 0
  Periodic = false
  PointList = -> [Sketch019]
  Polygonal = false
  StartOffset = 0
  Tangents = (9) [(0,-0.251607,-0.967829),(7.85413e-15,-0.190342,-0.981718),(-2.1326e-14,-0.145038,-0.989426),(1.87132e-17,-0.114739,-0.993396),+5 more]
  Tolerance = 1e-07
  UTurns = 0
  VTurns = 0
  WireOutput = false
FEATURE [Part::FeaturePython] Interpolation_Curve022  # WARN: FeaturePython — macro-defined, semantics opaque (R4)
  CustomTangents = false
  DetectAligned = false
  Parameters = [0,0.109883,0.217517,0.32404,0.430219,0.537507,0.653711,0.858179,1]
  Parametrization = 0
  Periodic = false
  PointList = -> [Sketch060]
  Polygonal = false
  StartOffset = 0
  Tangents = (9) [(-3.08307e-14,-0.329918,-0.944009),(1.54428e-14,-0.239351,-0.970933),(0,-0.171144,-0.985246),(-1.06214e-14,-0.125359,-0.992111),+5 more]
  Tolerance = 1e-07
  UTurns = 0
  VTurns = 0
  WireOutput = false
FEATURE [Part::FeaturePython] Interpolation_Curve023  # WARN: FeaturePython — macro-defined, semantics opaque (R4)
  CustomTangents = false
  DetectAligned = false
  Parameters = [0,0.126479,0.245964,0.363164,0.480233,0.59711,0.7164,0.946792,1]
  Parametrization = 0
  Periodic = false
  PointList = -> [Sketch023]
  Polygonal = false
  StartOffset = 0
  Tangents = (9) [(0,-0.495725,-0.868479),(0,-0.309366,-0.950943),(0,-0.17883,-0.98388),(0,-0.134111,-0.990966),(0,-0.133593,-0.991036),+4 more]
  Tolerance = 1e-07
  UTurns = 0
  VTurns = 0
  WireOutput = false
FEATURE [Sketcher::SketchObject] Sketch048
  AttachmentOffset = pos=(0,0,0.28956) rot=(0,0,1;0rad)
  ExternalGeometry = -> [Sketch013,Sketch009,Sketch012,Sketch011]
  FullyConstrained = true
  MapMode = 5
  Placement = pos=(0,0,0.28956) rot=(0,0,1;0rad)
  Support = -> [XY_Plane]
FEATURE [Sketcher::SketchObject] Sketch047
  ExternalGeometry = -> [Sketch010,Sketch013,Sketch008]
  FullyConstrained = false
  MapMode = 5
  Placement = pos=(0,0,0) rot=(1,0,0;1.5708rad)
  Support = -> [XZ_Plane]
  sketch-geometry (8):
    g0: GeomPoint X=0.01904 Y=0.22911 Z=0
    g1: GeomPoint X=0 Y=0.28956 Z=0
    g2: GeomPoint X=0.01904 Y=0.22911 Z=0
    g3: BSplineCurve PolesCount=4 KnotsCount=2 Degree=3 IsPeriodic=0
    g4-g7: Circle x4 (B-spline internal-alignment scaffolding for g3; pole/knot coordinates omitted)
  constraints (13):
    c: Coincident(g0,g-6)
    c: Coincident(g3,g-3)
    c: Coincident(g3,g0)
    c: InternalAlignment(g1,g3)
    c: InternalAlignment(g2,g3)
    c: InternalAlignment(g4,g3)
    c: Weight(g4) = 1
    c: InternalAlignment(g5,g3)
    c: Equal(g5,g4)
    c: InternalAlignment(g6,g3)
    c: Equal(g6,g4)
    c: InternalAlignment(g7,g3)
    c: Equal(g7,g4)
FEATURE [Sketcher::SketchObject] Sketch015
  AttachmentOffset = pos=(0,0,0.16724) rot=(0,0,1;0rad)
  ExternalGeometry = -> [Sketch047]
  FullyConstrained = false
  MapMode = 5
  Placement = pos=(0.16724,0,0) rot=(0.57735,0.57735,0.57735;2.0944rad)
  Support = -> [YZ_Plane]
  expr: Constraints[10] = Sketch008.Constraints[10]
  expr: Constraints[11] = Sketch008.Constraints[11]
  expr: Constraints[12] = Sketch008.Constraints[12]
  expr: Constraints[13] = Sketch008.Constraints[13]
  expr: Constraints[14] = Sketch008.Constraints[14]
  expr: Constraints[17] = Sketch008.Constraints[17]
  expr: Constraints[18] = Sketch008.Constraints[18]
  expr: Constraints[19] = Sketch008.Constraints[19]
  expr: Constraints[20] = Sketch008.Constraints[20]
  expr: Constraints[21] = Sketch008.Constraints[21]
  expr: Constraints[22] = Sketch008.Constraints[22]
  expr: Constraints[23] = Sketch008.Constraints[23]
  sketch-geometry (12):
    g0: LineSegment StartX=0 StartY=0.15 StartZ=0 EndX=0.003 EndY=0.15 EndZ=0
    g1: LineSegment StartX=0 StartY=0.18 StartZ=0 EndX=0.03677 EndY=0.18 EndZ=0
    g2: LineSegment StartX=0 StartY=0.21 StartZ=0 EndX=0.08149 EndY=0.21 EndZ=0
    g3: LineSegment StartX=0 StartY=0.24 StartZ=0 EndX=0.10547 EndY=0.24 EndZ=0
    g4: LineSegment StartX=0 StartY=0.28956 StartZ=0 EndX=0.13305 EndY=0.28956 EndZ=0
    g5: LineSegment StartX=0 StartY=0.27 StartZ=0 EndX=0.12303 EndY=0.27 EndZ=0
    g6: GeomPoint X=0 Y=0 Z=0
    g7: GeomPoint X=0 Y=0.12633 Z=0
    g8: GeomPoint X=0 Y=0.119754 Z=0
    g9: GeomPoint X=0 Y=0.089922 Z=0
    g10: GeomPoint X=0 Y=0.060364 Z=0
    g11: GeomPoint X=0 Y=0.029913 Z=0
  constraints (29):
    c: PointOnObject(g0,g-2)
    c: Horizontal(g0)
    c: PointOnObject(g1,g-2)
    c: Horizontal(g1)
    c: PointOnObject(g2,g-2)
    c: Horizontal(g2)
    c: PointOnObject(g3,g-2)
    c: Horizontal(g3)
    c: PointOnObject(g4,g-2)
    c: Horizontal(g4)
    c: DistanceY(g-1,g0) = 0.15
    c: DistanceY(g-1,g1) = 0.18
    c: DistanceY(g-1,g2) = 0.21
    c: DistanceY(g-1,g3) = 0.24
    c: DistanceY(g-1,g4) = 0.28956
    c: PointOnObject(g5,g-2)
    c: Horizontal(g5)
    c: DistanceY(g-1,g5) = 0.27
    c: DistanceX(g4,g4) = 0.13305
    c: DistanceX(g5,g5) = 0.12303
    c: DistanceX(g3,g3) = 0.10547
    c: DistanceX(g2,g2) = 0.08149
    c: DistanceX(g1,g1) = 0.03677
    c: DistanceX(g0,g0) = 0.003
    c: Coincident(g6,g-1)
    c: PointOnObject(g8,g-2)
    c: PointOnObject(g9,g-2)
    c: PointOnObject(g10,g-2)
    c: PointOnObject(g11,g-2)
FEATURE [Sketcher::SketchObject] Sketch059
  ExternalGeometry = -> [Sketch047]
  FullyConstrained = false
  MapMode = 5
  Placement = pos=(0,0,0) rot=(1,0,0;1.5708rad)
  Support = -> [XZ_Plane]
  sketch-geometry (1):
    g0: GeomPoint X=0 Y=0.28956 Z=0
FEATURE [Sketcher::SketchObject] Sketch053
  AttachmentOffset = pos=(0,0,0.28956) rot=(0,0,1;0rad)
  ExternalGeometry = -> [Sketch047]
  FullyConstrained = false
  MapMode = 5
  Placement = pos=(0,0,0.28956) rot=(0,0,1;0rad)
  Support = -> [XY_Plane]
  sketch-geometry (1):
    g0: LineSegment StartX=0 StartY=0 StartZ=0 EndX=0.16724 EndY=0 EndZ=0
FEATURE [PartDesign::Body] Body
  Group = -> [Sketch,Sketch001,Sketch003,Sketch004,Sketch005,Sketch006,Sketch007,Sketch008,Sketch009,Sketch010,Sketch011,Sketch012,Sketch013,Sketch014,Sketch015,Sketch016,Sketch017,Sketch018,Sketch019,Sketch020,Sketch023,Sketch026,Sketch028,Sketch029,Sketch042,Sketch047,Sketch048,Sketch050,Sketch052,Sketch053,Sketch055,Sketch057,Sketch058,Sketch059,Sketch060]
  Origin = -> Origin
FEATURE [Part::FeaturePython] Interpolation_Curve  # WARN: FeaturePython — macro-defined, semantics opaque (R4)
  CustomTangents = false
  DetectAligned = false
  Parameters = [0,0.063821,0.164767,0.276298,0.432679,0.563854,0.633141,0.652237,0.738869,0.824704,1]
  Parametrization = 0
  Periodic = false
  PointList = -> [Sketch015]
  Polygonal = false
  StartOffset = 0
  Tangents = (11) [(0,-0.447876,-0.894096),(-5.60379e-16,-0.469274,-0.883053),(7.65175e-16,-0.546146,-0.83769),(1.32693e-16,-0.725639,-0.688075),+7 more]
  Tolerance = 1e-07
  UTurns = 0
  VTurns = 0
  WireOutput = false
FEATURE [Part::FeaturePython] Interpolation_Curve026  # WARN: FeaturePython — macro-defined, semantics opaque (R4)
  CustomTangents = false
  DetectAligned = false
  Parameters = [0,0.295692,0.783829,1]
  Parametrization = 0
  Periodic = false
  PointList = -> [Sketch013]
  Polygonal = false
  StartOffset = 0
  Tangents = (4) [(0,-0.534146,-0.845392),(1.15389e-16,-0.551875,-0.833927),(-3.24177e-17,-0.713591,-0.700562),(-8.75605e-32,-0.818501,-0.574506)]
  Tolerance = 1e-07
  UTurns = 0
  VTurns = 0
  WireOutput = false
FEATURE [Part::FeaturePython] Interpolation_Curve028  # WARN: FeaturePython — macro-defined, semantics opaque (R4)
  CustomTangents = false
  DetectAligned = false
  Parameters = [0,0.149816,0.383912,0.641765,1]
  Parametrization = 0
  Periodic = false
  PointList = -> [Sketch012]
  Polygonal = false
  StartOffset = 0
  Tangents = (5) [(0,-0.46167,-0.887052),(0,-0.459584,-0.888134),(1.58102e-16,-0.529943,-0.848033),(-1.92631e-16,-0.704452,-0.709752),(7.27052e-16,-0.974339,-0.225087)]
  Tolerance = 1e-07
  UTurns = 0
  VTurns = 0
  WireOutput = false
FEATURE [Part::FeaturePython] Interpolation_Curve030  # WARN: FeaturePython — macro-defined, semantics opaque (R4)
  CustomTangents = false
  DetectAligned = false
  Parameters = [0,0.123655,0.318051,0.531885,0.849154,1]
  Parametrization = 0
  Periodic = false
  PointList = -> [Sketch014]
  Polygonal = false
  StartOffset = 0
  Tangents = (6) [(-3.80087e-15,-0.45195,-0.892043),(9.01158e-16,-0.463556,-0.886068),(-3.06168e-16,-0.531743,-0.846906),(-1.09958e-16,-0.721721,-0.692184),+2 more]
  Tolerance = 1e-07
  UTurns = 0
  VTurns = 0
  WireOutput = false
FEATURE [Part::FeaturePython] Interpolation_Curve031  # WARN: FeaturePython — macro-defined, semantics opaque (R4)
  CustomTangents = false
  DetectAligned = false
  Parameters = [0,0.179342,0.460241,0.776595,1]
  Parametrization = 0
  Periodic = false
  PointList = -> [Sketch009]
  Polygonal = false
  StartOffset = 0
  Tangents = (5) [(0,-0.478651,-0.878005),(0,-0.475366,-0.879788),(0,-0.548344,-0.836253),(1.8387e-16,-0.760472,-0.64937),(3.59282e-32,-0.938853,-0.344318)]
  Tolerance = 1e-07
  UTurns = 0
  VTurns = 0
  WireOutput = false
FEATURE [Part::FeaturePython] Interpolation_Curve032  # WARN: FeaturePython — macro-defined, semantics opaque (R4)
  CustomTangents = false
  DetectAligned = false
  Parameters = [0,0.134711,0.345515,0.577206,0.946687,1]
  Parametrization = 0
  Periodic = false
  PointList = -> [Sketch011]
  Polygonal = false
  StartOffset = 0
  Tangents = (6) [(0,-0.453834,-0.891086),(2.12214e-16,-0.456542,-0.889702),(-1.77152e-16,-0.522239,-0.852799),(2.15071e-16,-0.714661,-0.699471),+2 more]
  Tolerance = 1e-07
  UTurns = 0
  VTurns = 0
  WireOutput = false
FEATURE [Part::FeaturePython] Interpolation_Curve033  # WARN: FeaturePython — macro-defined, semantics opaque (R4)
  CustomTangents = false
  DetectAligned = false
  Parameters = [0,0.0978494,0.252618,0.423616,0.663376,0.864492,0.970721,1]
  Parametrization = 0
  Periodic = false
  PointList = -> [Sketch015]
  Polygonal = false
  StartOffset = 0
  Tangents = (8) [(3.79755e-15,-0.447876,-0.894096),(-1.4599e-15,-0.46927,-0.883055),(4.55999e-16,-0.546161,-0.83768),(0,-0.72561,-0.688106),(0,-0.868616,-0.495485),+3 more]
  Tolerance = 1e-07
  UTurns = 0
  VTurns = 0
  WireOutput = false
FEATURE [Surface::Sections] Surface
  NSections = -> [Sketch029,Sketch028,Sketch026,Interpolation_Curve023,Interpolation_Curve022,Interpolation_Curve018,Interpolation_Curve010,Interpolation_Curve009,Interpolation_Curve008,Interpolation_Curve007,Interpolation_Curve006,Interpolation_Curve005,Interpolation_Curve004,Interpolation_Curve003,Interpolation_Curve002,Interpolation_Curve001,Sketch007,Interpolation_Curve]
FEATURE [Surface::Sections] Surface001
  NSections = -> [Interpolation_Curve,Sketch007,Interpolation_Curve001,Interpolation_Curve002,Interpolation_Curve003,Interpolation_Curve004,Interpolation_Curve005,Interpolation_Curve006,Interpolation_Curve007,Interpolation_Curve008,Interpolation_Curve009,Interpolation_Curve010,Interpolation_Curve018,Interpolation_Curve022,Interpolation_Curve023,Sketch026,Sketch028,Sketch029]
FEATURE [Surface::Sections] Surface002
  NSections = -> [Interpolation_Curve033,Interpolation_Curve030,Interpolation_Curve032,Interpolation_Curve028,Interpolation_Curve031,Interpolation_Curve026,Sketch047]
FEATURE [Surface::Sections] Surface003
  NSections = -> [Sketch047,Interpolation_Curve026,Interpolation_Curve031,Interpolation_Curve028,Interpolation_Curve032,Interpolation_Curve030,Interpolation_Curve033]
FEATURE [Part::Mirroring] Part__Mirroring  label="Surface001 (Mirror #1)"
  Base = (0,0,0)
  Normal = (0,1,0)
  Source = -> Surface001
FEATURE [Part::Mirroring] Part__Mirroring001  label="Surface003 (Mirror #2)"
  Base = (0,0,0)
  Normal = (0,1,0)
  Source = -> Surface003
FEATURE [Surface::GeomFillSurface] Surface004
  BoundaryList = -> [Part__Mirroring,Surface001,Part__Mirroring001,Surface003]
  FillType = 0
FEATURE [Part::Compound] Compound
  Links = -> [Surface004,Body,Sketch002,Interpolation_Curve001,Interpolation_Curve002,Interpolation_Curve003,Interpolation_Curve004,Interpolation_Curve005,Interpolation_Curve006,Interpolation_Curve007,Interpolation_Curve008,Interpolation_Curve009,Interpolation_Curve010,Interpolation_Curve,Interpolation_Curve018,Interpolation_Curve022,Interpolation_Curve023,Interpolation_Curve026,Interpolation_Curve028,+44 more]
